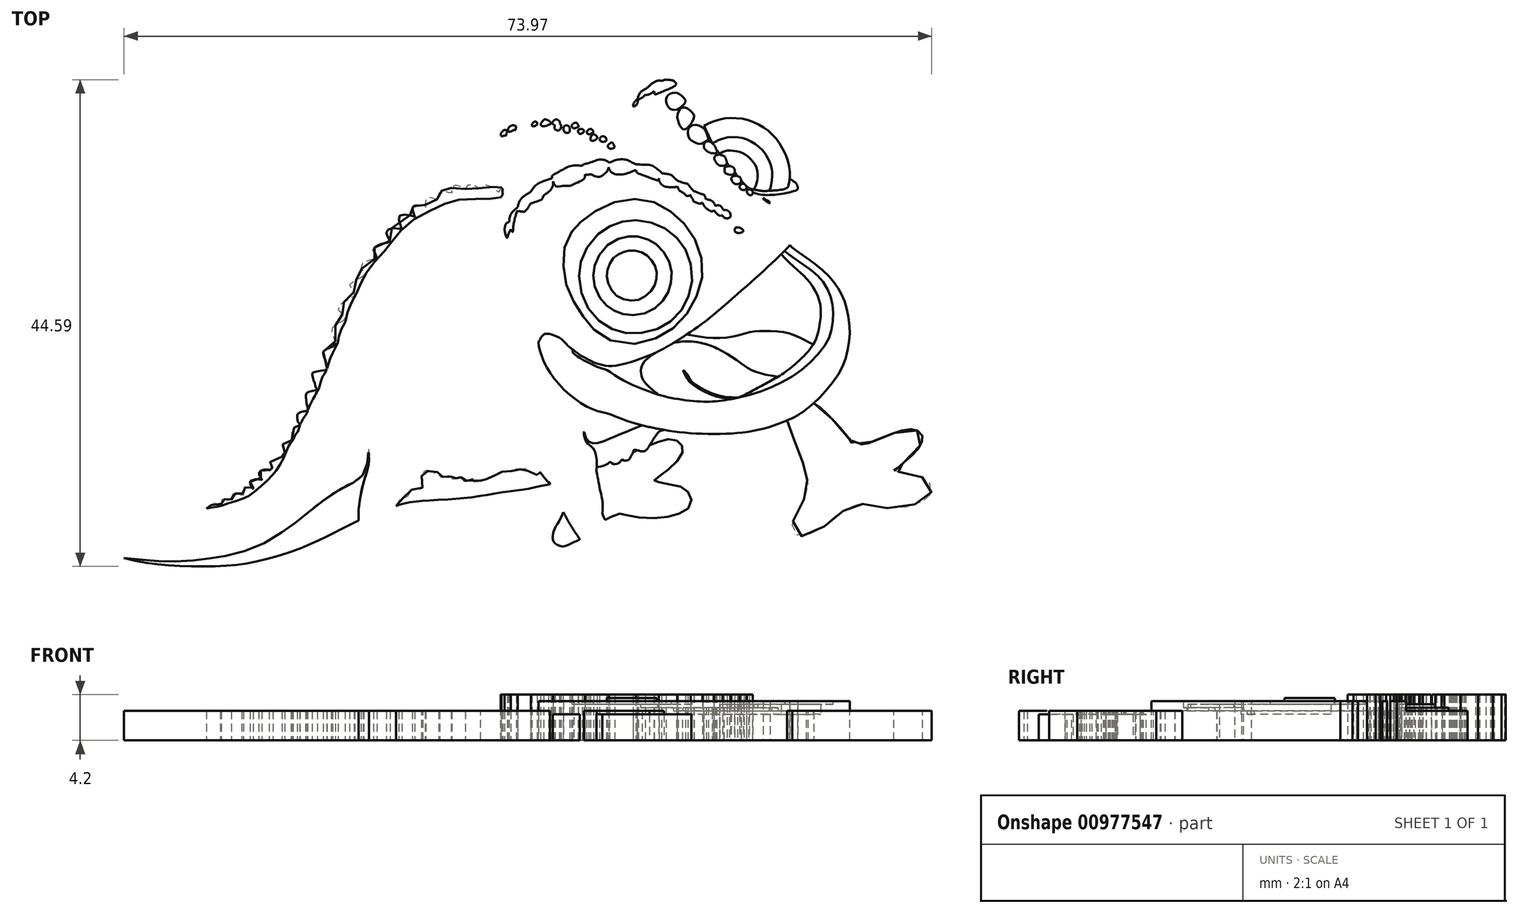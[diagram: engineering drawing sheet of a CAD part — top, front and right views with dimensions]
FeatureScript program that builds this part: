
annotation { "Feature Type Name" : "Feature", "Feature Type Description" : "" }
export const myFeature = defineFeature(function(context is Context, id is Id, definition is map)
    precondition{}
    {
        {
            var Q0;
            Q0=qCreatedBy(makeId("Top.planeOp"),FACE);
            var sketch = newSketch(context, id + "F0", { "sketchPlane" : qUnion([Q0])});
            skFitSpline(sketch, "E0", {"points": [v(3.36, 19.21) * mm, v(3.3, 19.55) * mm, v(3.25, 19.7) * mm, v(3.15, 20.16) * mm, v(3.22, 20.33) * mm, v(3.12, 20.54) * mm, v(3.1, 20.77) * mm, v(3.07, 20.9) * mm, v(3.13, 21.62) * mm, v(3.42, 22.28) * mm, v(3.48, 22.32) * mm, v(3.54, 22.32) * mm, v(3.5, 22.43) * mm, v(3.6, 22.71) * mm, v(3.91, 22.9) * mm, v(4.1, 22.82) * mm, v(4.13, 22.83) * mm, v(4.18, 23.04) * mm, v(4.6, 23.32) * mm, v(4.9, 23.23) * mm, v(4.98, 23.25) * mm, v(5.37, 23.44) * mm, v(5.56, 23.41) * mm, v(5.6, 23.45) * mm, v(5.75, 23.58) * mm, v(5.97, 23.6) * mm, v(6.16, 23.72) * mm, v(6.36, 23.71) * mm, v(6.58, 23.78) * mm, v(6.73, 23.79) * mm, v(6.85, 23.86) * mm, v(6.99, 23.79) * mm, v(7.13, 23.85) * mm, v(7.4, 23.84) * mm, v(7.43, 23.81) * mm, v(7.5, 23.85) * mm, v(7.77, 23.8) * mm, v(7.85, 23.77) * mm, v(7.97, 23.83) * mm, v(8.11, 23.77) * mm, v(8.21, 23.81) * mm, v(8.37, 23.77) * mm, v(8.6, 23.86) * mm, v(8.86, 23.7) * mm, v(8.96, 23.72) * mm, v(9.02, 23.7) * mm, v(9.66, 23.52) * mm, v(9.7, 23.5) * mm, v(9.8, 23.56) * mm, v(9.94, 23.45) * mm, v(10.06, 23.43) * mm, v(10.29, 23.54) * mm, v(10.47, 23.5) * mm, v(10.61, 23.3) * mm, v(10.72, 23.27) * mm, v(11.48, 22.95) * mm, v(11.55, 22.93) * mm, v(11.75, 22.98) * mm, v(11.93, 22.84) * mm, v(11.98, 22.73) * mm, v(12.04, 22.73) * mm, v(12.52, 22.87) * mm, v(14.39, 23.93) * mm, v(15.12, 24.58) * mm, v(15.61, 25.1) * mm, v(15.65, 25.3) * mm, v(16, 25.73) * mm, v(16.03, 25.76) * mm, v(16.1, 26.02) * mm, v(16.36, 26.4) * mm, v(16.61, 26.56) * mm, v(16.98, 26.8) * mm, v(17.36, 27.16) * mm, v(17.8, 27.38) * mm, v(18.13, 27.42) * mm, v(18.21, 27.39) * mm, v(18.5, 27.48) * mm, v(19.05, 27.46) * mm, v(19.4, 27.33) * mm, v(19.8, 26.81) * mm, v(19.97, 26.7) * mm, v(20.08, 26.52) * mm, v(20.3, 26.37) * mm, v(20.47, 26.08) * mm, v(20.68, 25.88) * mm, v(20.84, 25.53) * mm, v(20.98, 25.43) * mm, v(21.36, 24.69) * mm, v(21.85, 23.7) * mm, v(22.06, 23.33) * mm, v(22.1, 23.3) * mm, v(22.23, 23.34) * mm, v(22.63, 23.53) * mm, v(23.67, 23.88) * mm, v(24.92, 23.97) * mm, v(26.07, 23.82) * mm, v(27.24, 23.3) * mm, v(28.18, 22.64) * mm, v(28.92, 21.8) * mm, v(29.64, 20.47) * mm, v(29.96, 19.2) * mm, v(29.94, 18.42) * mm, v(29.95, 18.36) * mm, v(30.04, 18.34) * mm, v(30.26, 18.21) * mm, v(30.5, 18.03) * mm, v(30.66, 17.76) * mm, v(30.7, 17.54) * mm, v(30.7, 17.5) * mm, v(30.85, 17.46) * mm, v(31.15, 17.32) * mm, v(31.5, 16.97) * mm, v(31.79, 16.44) * mm, v(31.9, 15.87) * mm, v(31.7, 14.93) * mm, v(31.15, 13.83) * mm, v(30.33, 12.75) * mm, v(30, 12.37) * mm, v(29.98, 12.33) * mm, v(30.07, 12.21) * mm, v(31.05, 11.47) * mm, v(32.59, 10.36) * mm, v(33.74, 9.25) * mm, v(34.4, 8.36) * mm, v(34.9, 7.38) * mm, v(35.26, 6.15) * mm, v(35.44, 4.64) * mm, v(35.41, 3.6) * mm, v(35.09, 1.98) * mm, v(34.46, 0.58) * mm, v(33.14, -1.16) * mm, v(32.17, -2.13) * mm, v(31, -3.05) * mm, v(29.29, -3.9) * mm, v(26.88, -4.63) * mm, v(24.12, -4.95) * mm, v(20.81, -4.89) * mm, v(18.07, -4.53) * mm, v(14.95, -3.75) * mm, v(13.35, -3.12) * mm, v(12.18, -2.8) * mm, v(10.2, -1.7) * mm, v(8.22, 0.33) * mm, v(7.24, 2.16) * mm, v(6.96, 3.44) * mm, v(7.04, 4.02) * mm, v(6.96, 4.42) * mm, v(6.87, 4.52) * mm, v(6.86, 4.68) * mm, v(6.77, 4.8) * mm, v(6.81, 4.93) * mm, v(6.68, 5.06) * mm, v(6.64, 5.16) * mm, v(6.54, 5.27) * mm, v(6.53, 5.4) * mm, v(6.4, 5.52) * mm, v(6.4, 5.65) * mm, v(6.3, 5.75) * mm, v(6.28, 5.9) * mm, v(6.16, 5.97) * mm, v(6.05, 6.23) * mm, v(5.88, 6.37) * mm, v(5.87, 6.56) * mm, v(5.73, 6.72) * mm, v(5.53, 7.05) * mm, v(5.42, 7.08) * mm, v(5.38, 7.26) * mm, v(5.23, 7.33) * mm, v(5.18, 7.57) * mm, v(4.95, 7.62) * mm, v(4.85, 7.92) * mm, v(4.73, 8.04) * mm, v(4.57, 8.31) * mm, v(4.44, 8.38) * mm, v(4.25, 8.76) * mm, v(3.99, 9.34) * mm, v(3.65, 10.21) * mm, v(3.46, 10.94) * mm, v(3.4, 11.48) * mm, v(3.45, 12.23) * mm, v(3.5, 12.35) * mm, v(3.47, 12.52) * mm, v(3.5, 12.85) * mm, v(3.57, 12.92) * mm, v(3.52, 13.13) * mm, v(3.58, 13.32) * mm, v(3.55, 13.42) * mm, v(3.7, 13.73) * mm, v(3.62, 13.9) * mm, v(3.61, 14.08) * mm, v(3.74, 14.25) * mm, v(3.67, 14.43) * mm, v(3.67, 14.55) * mm, v(3.77, 14.7) * mm, v(3.7, 14.84) * mm, v(3.67, 15.05) * mm, v(3.72, 15.17) * mm, v(3.62, 15.47) * mm, v(3.58, 15.63) * mm, v(3.64, 15.75) * mm, v(3.56, 15.93) * mm, v(3.58, 16.1) * mm, v(3.67, 16.27) * mm, v(3.6, 16.48) * mm, v(3.51, 16.7) * mm, v(3.63, 16.91) * mm, v(3.66, 17.05) * mm, v(3.64, 17.33) * mm, v(3.68, 17.4) * mm, v(3.57, 17.6) * mm, v(3.5, 17.83) * mm, v(3.5, 18.02) * mm, v(3.44, 18.17) * mm, v(3.46, 18.36) * mm, v(3.4, 18.52) * mm, v(3.38, 18.72) * mm, v(3.43, 19) * mm, v(3.38, 19.14) * mm, v(3.36, 19.21) * mm]});
            skFitSpline(sketch, "E1", {"points": [v(22.1, 23.3) * mm, v(22.63, 22.16) * mm, v(22.8, 21.8) * mm, v(22.92, 21.6) * mm, v(23.04, 21.5) * mm, v(23.27, 21.02) * mm, v(23.33, 20.97) * mm, v(23.42, 20.86) * mm, v(23.43, 20.81) * mm, v(23.52, 20.76) * mm, v(23.54, 20.64) * mm, v(23.9, 20.52) * mm, v(24.12, 20.21) * mm, v(24.21, 19.89) * mm, v(24.3, 19.72) * mm, v(24.44, 19.57) * mm, v(24.55, 19.57) * mm, v(24.68, 19.51) * mm, v(24.82, 19.43) * mm, v(24.91, 19.22) * mm, v(24.93, 19.06) * mm, v(25.03, 18.86) * mm, v(25.16, 18.66) * mm, v(25.31, 18.62) * mm, v(25.42, 18.52) * mm, v(25.59, 18.16) * mm, v(25.84, 17.89) * mm, v(26.2, 17.57) * mm, v(26.8, 17.4) * mm, v(27.44, 17.3) * mm, v(28.2, 17.32) * mm, v(29.05, 17.4) * mm, v(29.64, 17.54) * mm, v(29.8, 17.65) * mm, v(29.84, 17.82) * mm, v(29.92, 18.2) * mm, v(29.95, 18.36) * mm], "startDerivative": vector(10.3, -22.36) * mm, "endDerivative": vector(1.64, 8.1) * mm});
            skFitSpline(sketch, "E2", {"points": [v(29.98, 12.33) * mm, v(29.51, 11.83) * mm, v(28.13, 10.5) * mm, v(25.13, 7.82) * mm, v(22.15, 5.3) * mm, v(20.12, 3.88) * mm, v(17.84, 2.57) * mm, v(15.15, 1.55) * mm, v(13.48, 1.25) * mm, v(12.74, 1.37) * mm, v(12, 1.6) * mm, v(10.98, 2.12) * mm, v(10.54, 2.43) * mm, v(10.18, 2.66) * mm, v(10.13, 2.66) * mm, v(10.04, 2.6) * mm, v(10.2, 2.38) * mm, v(10.67, 2.03) * mm, v(11.44, 1.6) * mm, v(12.67, 1.05) * mm, v(13.23, 0.87) * mm, v(14.13, 0.29) * mm, v(15.42, -0.41) * mm, v(16.91, -1.02) * mm, v(18.6, -1.56) * mm, v(21.65, -2) * mm, v(23.71, -1.92) * mm, v(26.07, -1.44) * mm, v(28.23, -0.7) * mm, v(30.3, 0.4) * mm, v(32.04, 1.78) * mm, v(33.3, 3.33) * mm, v(33.76, 4.53) * mm, v(33.95, 5.87) * mm, v(33.86, 6.97) * mm, v(33.54, 8.03) * mm, v(32.86, 9.18) * mm, v(31.95, 10) * mm, v(30.53, 11) * mm, v(29.72, 11.6) * mm, v(29.52, 11.77) * mm], "startDerivative": vector(-23.28, -25.11) * mm, "endDerivative": vector(-11.86, 14.14) * mm});
            skLineSegment(sketch, "E3", {"start": v(29.52, 11.77) * mm, "end": v(29.49, 11.8) * mm});
            skFitSpline(sketch, "E4", {"points": [v(14.66, 14.5) * mm, v(15.84, 14.61) * mm, v(17.45, 14.33) * mm, v(18.8, 13.67) * mm, v(19.97, 12.58) * mm, v(20.68, 11.35) * mm, v(21.02, 9.5) * mm, v(20.74, 7.86) * mm, v(20, 6.32) * mm, v(18.77, 5.13) * mm, v(17.34, 4.47) * mm, v(15.5, 4.25) * mm, v(14.1, 4.48) * mm, v(12.62, 5.29) * mm, v(11.45, 6.62) * mm, v(10.75, 8.45) * mm, v(10.7, 10.2) * mm, v(11.12, 11.62) * mm, v(12.32, 13.24) * mm, v(13.54, 14.1) * mm, v(14.66, 14.5) * mm]});
            skFitSpline(sketch, "E5", {"points": [v(32.17, -2.13) * mm, v(32.66, -2.47) * mm, v(33.56, -3.33) * mm, v(34.46, -4.25) * mm, v(35.37, -5.35) * mm, v(35.6, -5.72) * mm, v(35.62, -5.76) * mm, v(35.7, -5.73) * mm, v(35.9, -5.68) * mm, v(36.13, -5.73) * mm, v(36.33, -5.84) * mm, v(36.4, -5.98) * mm, v(36.46, -5.93) * mm, v(36.76, -5.9) * mm, v(37.41, -5.73) * mm, v(38.35, -5.32) * mm, v(39.02, -5.08) * mm, v(40.07, -4.7) * mm, v(41.05, -4.51) * mm, v(41.64, -4.66) * mm, v(42.03, -5.01) * mm, v(42.12, -5.37) * mm, v(41.98, -5.9) * mm, v(41.47, -6.63) * mm, v(40.62, -7.4) * mm, v(39.86, -8.06) * mm, v(39.55, -8.27) * mm, v(39.5, -8.3) * mm, v(39.65, -8.33) * mm, v(40.23, -8.53) * mm, v(41.69, -8.82) * mm, v(42.1, -8.96) * mm, v(42.58, -9.3) * mm, v(42.9, -9.78) * mm, v(42.93, -10.3) * mm, v(42.71, -10.8) * mm, v(42.22, -11.1) * mm, v(40.92, -11.59) * mm, v(39.88, -11.76) * mm, v(38.26, -11.7) * mm, v(37.2, -11.47) * mm, v(36.6, -11.38) * mm, v(36.05, -11.41) * mm, v(35.23, -11.8) * mm, v(34.58, -12.19) * mm, v(33.75, -12.9) * mm, v(32.97, -13.54) * mm, v(31.99, -14.05) * mm, v(31.12, -14.34) * mm, v(30.45, -14.13) * mm, v(30.21, -13.6) * mm, v(30.29, -12.83) * mm, v(30.8, -11.93) * mm, v(31.26, -10.99) * mm, v(31.59, -9.9) * mm, v(31.66, -9.54) * mm, v(31.57, -9.26) * mm, v(31.48, -8.78) * mm, v(31.46, -8.26) * mm, v(31.25, -7.84) * mm, v(30.85, -6.89) * mm, v(30.46, -5.85) * mm, v(30.21, -5.05) * mm, v(29.84, -4.02) * mm, v(29.72, -3.77) * mm, v(29.7, -3.74) * mm], "startDerivative": vector(30.93, -18.84) * mm, "endDerivative": vector(-5.35, 12.51) * mm});
            skFitSpline(sketch, "E6", {"points": [v(17.12, -6.01) * mm, v(17.73, -5.76) * mm, v(18.57, -5.48) * mm, v(19.33, -5.47) * mm, v(19.77, -5.69) * mm, v(20.08, -6.02) * mm, v(20.15, -6.39) * mm, v(20.1, -6.84) * mm, v(19.51, -7.6) * mm, v(18.62, -8.4) * mm, v(18.03, -8.84) * mm, v(17.63, -9.17) * mm, v(17.54, -9.24) * mm, v(17.63, -9.27) * mm, v(18.1, -9.43) * mm, v(19.26, -9.64) * mm, v(20.04, -9.84) * mm, v(20.55, -10.2) * mm, v(20.91, -10.73) * mm, v(20.87, -11.47) * mm, v(20.4, -12.02) * mm, v(19.4, -12.4) * mm, v(18.3, -12.63) * mm, v(16.43, -12.66) * mm, v(15.3, -12.46) * mm, v(14.56, -12.28) * mm, v(14.24, -12.3) * mm, v(13.48, -12.61) * mm, v(13.09, -12.83) * mm, v(13.05, -12.85) * mm, v(13, -12.75) * mm, v(12.81, -12.3) * mm, v(12.84, -11.66) * mm, v(12.68, -10.48) * mm, v(12.51, -9.74) * mm, v(12.3, -8.63) * mm, v(12.27, -8.08) * mm, v(12.62, -7.95) * mm, v(13.14, -7.8) * mm, v(13.44, -7.59) * mm, v(13.56, -7.54) * mm, v(13.75, -7.71) * mm, v(14.05, -7.72) * mm, v(14.36, -7.6) * mm, v(14.49, -7.41) * mm, v(14.6, -7.33) * mm, v(14.86, -7.43) * mm, v(15.06, -7.39) * mm, v(15.28, -7.28) * mm, v(15.4, -7.05) * mm, v(15.6, -6.64) * mm, v(15.67, -6.45) * mm, v(15.96, -6.45) * mm, v(16.43, -6.57) * mm, v(16.74, -6.49) * mm, v(17.02, -6.17) * mm, v(17.12, -6.01) * mm]});
            skFitSpline(sketch, "E7", {"points": [v(9.21, -12.15) * mm, v(9.2, -12.22) * mm, v(9.07, -12.5) * mm, v(8.76, -13.09) * mm, v(8.46, -13.57) * mm, v(8.31, -13.98) * mm, v(8.24, -14.5) * mm, v(8.37, -14.88) * mm, v(8.7, -15.16) * mm, v(9.26, -15.28) * mm, v(9.8, -15.08) * mm, v(10.35, -14.81) * mm, v(10.7, -14.65) * mm, v(10.74, -14.63) * mm, v(10.7, -14.57) * mm, v(10.4, -14.15) * mm, v(10.02, -13.55) * mm, v(9.7, -13.03) * mm, v(9.44, -12.53) * mm, v(9.26, -12.19) * mm, v(9.21, -12.15) * mm]});
            skFitSpline(sketch, "E8", {"points": [v(15.6, -6.64) * mm, v(15.8, -6.57) * mm, v(16.01, -6.47) * mm], "startDerivative": vector(0.38, 0.15) * mm, "endDerivative": vector(0.42, 0.2) * mm});
            skFitSpline(sketch, "E9", {"points": [v(17.12, -6.01) * mm, v(17.35, -5.63) * mm, v(17.7, -5.12) * mm, v(17.96, -4.79) * mm, v(18.2, -4.65) * mm, v(18.43, -4.6) * mm], "startDerivative": vector(0.97, 1.7) * mm, "endDerivative": vector(1.43, 0.4) * mm});
            skFitSpline(sketch, "E10", {"points": [v(13.05, -12.85) * mm, v(13.4, -13.6) * mm, v(13.92, -14.65) * mm, v(14.3, -15.25) * mm, v(14.83, -15.89) * mm, v(15.55, -16.82) * mm, v(16.03, -17.45) * mm, v(16.54, -17.98) * mm, v(16.8, -18.2) * mm, v(17.09, -18.54) * mm, v(17.3, -18.9) * mm, v(17.49, -19.25) * mm, v(17.59, -19.46) * mm, v(17.62, -19.5) * mm, v(17.72, -19.53) * mm, v(18, -19.74) * mm, v(18.29, -19.92) * mm, v(18.67, -20.05) * mm, v(19.2, -20.03) * mm, v(19.94, -19.97) * mm, v(20.93, -19.76) * mm, v(21.74, -19.57) * mm, v(22.27, -19.59) * mm, v(22.65, -19.68) * mm, v(22.95, -19.84) * mm, v(23.17, -20.07) * mm, v(23.28, -20.35) * mm, v(23.28, -20.67) * mm, v(23.22, -20.88) * mm, v(23.06, -21.2) * mm, v(22.46, -21.93) * mm, v(21.92, -22.64) * mm, v(21.26, -23.31) * mm, v(20.64, -23.75) * mm, v(20.04, -24.22) * mm, v(19.43, -24.8) * mm, v(18.99, -25.18) * mm, v(18.86, -25.3) * mm, v(18.75, -25.6) * mm, v(18.7, -25.98) * mm, v(18.6, -26.82) * mm, v(18.33, -27.68) * mm, v(17.88, -28.37) * mm, v(17.35, -28.83) * mm, v(16.71, -29.2) * mm, v(15.83, -29.46) * mm, v(14.95, -29.4) * mm, v(14.37, -29.2) * mm, v(14.03, -28.71) * mm, v(13.97, -28.15) * mm, v(14.14, -27.4) * mm, v(14.28, -26.68) * mm, v(14.27, -26.65) * mm, v(14.1, -26.73) * mm, v(13.35, -26.98) * mm, v(12.23, -27.26) * mm, v(11, -27.52) * mm, v(9.8, -27.57) * mm, v(9.23, -27.47) * mm, v(8.95, -27.22) * mm, v(8.84, -26.8) * mm, v(8.94, -26.3) * mm, v(9.22, -25.87) * mm, v(9.74, -25.46) * mm, v(10.36, -25.07) * mm, v(10.86, -24.7) * mm, v(11.47, -24.33) * mm, v(12.13, -23.97) * mm, v(12.7, -23.65) * mm, v(13.1, -23.33) * mm, v(13.25, -23.2) * mm, v(13.23, -23.14) * mm, v(13.22, -22.92) * mm, v(13.28, -22.58) * mm, v(13.35, -22.43) * mm, v(13.33, -22.39) * mm, v(13.11, -22) * mm, v(12.81, -21.3) * mm, v(12.64, -20.71) * mm, v(12.4, -20.15) * mm, v(12, -19.22) * mm, v(11.67, -18.32) * mm, v(11.44, -17.49) * mm, v(11.32, -16.6) * mm, v(11.27, -16.02) * mm, v(11.3, -15.63) * mm, v(11.27, -15.57) * mm, v(11.04, -15.1) * mm, v(10.85, -14.79) * mm, v(10.74, -14.63) * mm], "startDerivative": vector(22.88, -50.93) * mm, "endDerivative": vector(-15.94, 22.2) * mm});
            skFitSpline(sketch, "E11", {"points": [v(3.57, 17.6) * mm, v(3.52, 17.54) * mm, v(3.53, 17.45) * mm, v(3.49, 17.4) * mm, v(3.38, 17.33) * mm, v(3.32, 17.22) * mm, v(3.31, 17.15) * mm, v(3.29, 17.18) * mm, v(3.06, 17.4) * mm, v(2.58, 17.76) * mm, v(2.2, 17.83) * mm, v(1.9, 17.75) * mm, v(1.73, 17.55) * mm, v(1.69, 17.46) * mm, v(1.67, 17.4) * mm, v(1.6, 17.47) * mm, v(1.42, 17.58) * mm, v(1.06, 17.8) * mm, v(0.78, 17.87) * mm, v(0.5, 17.83) * mm, v(0.33, 17.74) * mm, v(0.26, 17.58) * mm, v(0.26, 17.47) * mm, v(0.24, 17.46) * mm, v(0.13, 17.52) * mm, v(-0.08, 17.67) * mm, v(-0.42, 17.8) * mm, v(-0.75, 17.81) * mm, v(-0.93, 17.72) * mm, v(-1.04, 17.6) * mm, v(-1.06, 17.37) * mm, v(-1, 17.1) * mm, v(-1, 16.96) * mm, v(-1.02, 16.98) * mm, v(-1.44, 17.24) * mm, v(-1.76, 17.34) * mm, v(-2, 17.3) * mm, v(-2.15, 17.16) * mm, v(-2.2, 16.9) * mm, v(-2.16, 16.58) * mm, v(-2.13, 16.41) * mm, v(-2.12, 16.37) * mm, v(-2.17, 16.41) * mm, v(-2.28, 16.49) * mm, v(-2.72, 16.66) * mm, v(-3.11, 16.66) * mm, v(-3.29, 16.6) * mm, v(-3.4, 16.49) * mm, v(-3.43, 16.38) * mm, v(-3.45, 16.17) * mm, v(-3.4, 15.92) * mm, v(-3.37, 15.82) * mm, v(-3.37, 15.79) * mm, v(-3.45, 15.83) * mm, v(-3.67, 15.9) * mm, v(-4, 16) * mm, v(-4.33, 15.97) * mm, v(-4.54, 15.86) * mm, v(-4.6, 15.72) * mm, v(-4.61, 15.55) * mm, v(-4.52, 15.3) * mm, v(-4.43, 15.09) * mm, v(-4.38, 14.95) * mm, v(-4.4, 14.96) * mm, v(-4.75, 15.04) * mm, v(-5.13, 15.11) * mm, v(-5.5, 15.11) * mm, v(-5.72, 15.04) * mm, v(-5.8, 14.93) * mm, v(-5.85, 14.76) * mm, v(-5.8, 14.5) * mm, v(-5.71, 14.22) * mm, v(-5.6, 13.94) * mm, v(-5.58, 13.84) * mm, v(-5.57, 13.8) * mm, v(-5.61, 13.79) * mm, v(-5.8, 13.82) * mm, v(-6.24, 13.9) * mm, v(-6.6, 13.85) * mm, v(-6.86, 13.73) * mm, v(-6.97, 13.6) * mm, v(-7, 13.45) * mm, v(-6.91, 13.2) * mm, v(-6.76, 12.92) * mm, v(-6.67, 12.7) * mm, v(-6.65, 12.64) * mm, v(-6.7, 12.62) * mm, v(-6.93, 12.54) * mm, v(-7.38, 12.45) * mm, v(-7.7, 12.33) * mm, v(-8.01, 12.18) * mm, v(-8.12, 12.07) * mm, v(-8.15, 11.9) * mm, v(-8.1, 11.77) * mm, v(-7.97, 11.44) * mm, v(-7.85, 11.2) * mm, v(-7.87, 11.18) * mm, v(-7.97, 11.13) * mm, v(-8, 11.09) * mm, v(-8.06, 11.05) * mm, v(-8.25, 11.01) * mm, v(-8.64, 10.93) * mm, v(-9.11, 10.7) * mm, v(-9.24, 10.56) * mm, v(-9.3, 10.36) * mm, v(-9.25, 10.14) * mm, v(-9.09, 9.82) * mm, v(-9.05, 9.68) * mm, v(-9.09, 9.58) * mm, v(-9.13, 9.46) * mm, v(-9.14, 9.4) * mm, v(-9.23, 9.36) * mm, v(-9.67, 9.17) * mm, v(-10.06, 8.98) * mm, v(-10.26, 8.85) * mm, v(-10.35, 8.69) * mm, v(-10.34, 8.47) * mm, v(-10.16, 8.26) * mm, v(-10.06, 8.13) * mm, v(-9.9, 7.89) * mm, v(-9.91, 7.83) * mm, v(-9.95, 7.76) * mm, v(-9.95, 7.64) * mm, v(-10, 7.6) * mm, v(-10.1, 7.54) * mm, v(-10.54, 7.34) * mm, v(-10.87, 7.12) * mm, v(-11.1, 6.94) * mm, v(-11.3, 6.77) * mm, v(-11.4, 6.62) * mm, v(-11.41, 6.48) * mm, v(-11.3, 6.27) * mm, v(-11.11, 6.07) * mm, v(-10.9, 5.82) * mm, v(-10.77, 5.66) * mm, v(-10.76, 5.63) * mm, v(-10.78, 5.6) * mm, v(-10.87, 5.47) * mm, v(-11, 5.36) * mm, v(-11.44, 5.14) * mm, v(-11.77, 4.87) * mm, v(-11.99, 4.68) * mm, v(-12.05, 4.47) * mm, v(-11.96, 4.23) * mm, v(-11.8, 3.9) * mm, v(-11.7, 3.58) * mm, v(-11.66, 3.5) * mm, v(-11.76, 3.22) * mm, v(-11.82, 3.07) * mm, v(-11.95, 3.02) * mm, v(-12.23, 2.9) * mm, v(-12.58, 2.72) * mm, v(-12.77, 2.53) * mm, v(-12.73, 2.24) * mm, v(-12.6, 1.86) * mm, v(-12.5, 1.6) * mm, v(-12.47, 1.37) * mm, v(-12.45, 1.2) * mm, v(-12.43, 1.03) * mm, v(-12.52, 0.92) * mm, v(-12.78, 0.84) * mm, v(-13.28, 0.78) * mm, v(-13.61, 0.68) * mm, v(-13.73, 0.64) * mm, v(-13.77, 0.52) * mm, v(-13.72, 0.24) * mm, v(-13.63, -0.09) * mm, v(-13.52, -0.41) * mm, v(-13.47, -0.7) * mm, v(-13.36, -0.8) * mm, v(-13.3, -0.92) * mm, v(-13.46, -0.98) * mm, v(-13.8, -1.03) * mm, v(-14.15, -1.14) * mm, v(-14.31, -1.26) * mm, v(-14.37, -1.43) * mm, v(-14.37, -1.6) * mm, v(-14.3, -1.98) * mm, v(-14.28, -2.27) * mm, v(-14.19, -2.5) * mm, v(-14.21, -2.7) * mm, v(-14.2, -2.83) * mm, v(-14.34, -2.87) * mm, v(-14.68, -2.93) * mm, v(-14.97, -3.04) * mm, v(-15.13, -3.2) * mm, v(-15.15, -3.5) * mm, v(-15.09, -3.83) * mm, v(-14.98, -4) * mm, v(-14.9, -4.08) * mm, v(-14.89, -4.13) * mm, v(-14.94, -4.16) * mm, v(-14.93, -4.22) * mm, v(-15, -4.24) * mm, v(-15.33, -4.36) * mm, v(-15.62, -4.54) * mm, v(-15.7, -4.72) * mm, v(-15.64, -5.05) * mm, v(-15.54, -5.33) * mm, v(-15.6, -5.35) * mm, v(-15.64, -5.4) * mm, v(-15.68, -5.48) * mm, v(-15.66, -5.55) * mm, v(-15.7, -5.55) * mm, v(-16.1, -5.72) * mm, v(-16.42, -5.89) * mm, v(-16.54, -6.03) * mm, v(-16.48, -6.27) * mm, v(-16.34, -6.6) * mm, v(-16.3, -6.74) * mm, v(-16.42, -6.83) * mm, v(-16.46, -6.92) * mm, v(-16.48, -7.02) * mm, v(-16.72, -7.12) * mm, v(-17.43, -7.4) * mm, v(-17.66, -7.58) * mm, v(-17.74, -7.71) * mm, v(-17.67, -7.9) * mm, v(-17.5, -8) * mm, v(-17.4, -8.15) * mm, v(-17.4, -8.24) * mm, v(-17.47, -8.22) * mm, v(-17.5, -8.26) * mm, v(-17.55, -8.3) * mm, v(-17.77, -8.25) * mm, v(-18.1, -8.22) * mm, v(-18.39, -8.3) * mm, v(-18.6, -8.43) * mm, v(-18.66, -8.62) * mm, v(-18.56, -8.86) * mm, v(-18.41, -9.08) * mm, v(-18.39, -9.17) * mm, v(-18.45, -9.17) * mm, v(-18.73, -9.13) * mm, v(-18.96, -9.13) * mm, v(-19.19, -9.18) * mm, v(-19.42, -9.27) * mm, v(-19.48, -9.4) * mm, v(-19.4, -9.63) * mm, v(-19.26, -9.82) * mm, v(-19.2, -9.85) * mm, v(-19.18, -9.92) * mm, v(-19.21, -10) * mm, v(-19.34, -9.95) * mm, v(-19.8, -9.87) * mm, v(-20.1, -9.9) * mm, v(-20.21, -10.03) * mm, v(-20.19, -10.3) * mm, v(-20.06, -10.57) * mm, v(-20.14, -10.62) * mm, v(-20.82, -10.45) * mm, v(-20.95, -10.45) * mm, v(-21.13, -10.56) * mm, v(-21.19, -10.82) * mm, v(-21.21, -11.06) * mm, v(-21.33, -11.14) * mm, v(-21.53, -11.05) * mm, v(-21.86, -10.95) * mm, v(-22, -10.97) * mm, v(-22.09, -11.05) * mm, v(-22.12, -11.26) * mm, v(-22.11, -11.4) * mm, v(-22.16, -11.4) * mm, v(-22.21, -11.44) * mm, v(-22.2, -11.5) * mm, v(-22.25, -11.52) * mm, v(-22.32, -11.45) * mm, v(-22.62, -11.35) * mm, v(-22.76, -11.33) * mm, v(-22.95, -11.43) * mm, v(-23.08, -11.52) * mm, v(-23.32, -11.68) * mm, v(-23.43, -11.7) * mm, v(-23.49, -11.75) * mm, v(-23.47, -11.81) * mm, v(-23.53, -11.8) * mm, v(-23.64, -11.82) * mm, v(-23.78, -11.89) * mm, v(-24.05, -11.84) * mm, v(-24.3, -11.92) * mm, v(-24.4, -11.88) * mm, v(-24.63, -11.98) * mm, v(-24.71, -11.9) * mm, v(-24.86, -11.91) * mm, v(-24.9, -12.01) * mm, v(-25.01, -12.03) * mm, v(-25.1, -11.94) * mm, v(-25.26, -12.04) * mm, v(-25.39, -11.98) * mm, v(-25.62, -12.1) * mm, v(-25.75, -12.04) * mm, v(-25.92, -12.12) * mm, v(-26.11, -12.09) * mm, v(-26.25, -12.18) * mm, v(-26.37, -12.09) * mm, v(-26.52, -12.2) * mm, v(-26.67, -12.13) * mm, v(-26.78, -12.21) * mm, v(-26.95, -12.13) * mm, v(-27.1, -12.22) * mm, v(-27.38, -12.16) * mm, v(-27.88, -12.17) * mm, v(-28.73, -12.12) * mm, v(-30.06, -11.96) * mm, v(-31.97, -11.46) * mm, v(-34.52, -10.39) * mm, v(-36.83, -8.78) * mm, v(-38.21, -7.47) * mm, v(-39.16, -6.46) * mm, v(-40.37, -5.2) * mm, v(-41.08, -4.16) * mm, v(-41.6, -2.48) * mm, v(-41.47, -0.75) * mm, v(-41.01, 0.46) * mm, v(-40.08, 1.58) * mm, v(-39, 2.24) * mm, v(-38.02, 2.54) * mm, v(-36.34, 2.46) * mm, v(-35.03, 1.53) * mm, v(-34.26, 0.26) * mm, v(-34.01, -1.1) * mm, v(-34.2, -2.59) * mm, v(-35.31, -4.2) * mm, v(-36.95, -4.68) * mm, v(-38.44, -4.23) * mm, v(-39.01, -3.73) * mm, v(-39.59, -2.54) * mm, v(-39.53, -1) * mm, v(-38.9, 0.08) * mm, v(-37.9, 0.66) * mm, v(-36.77, 0.77) * mm, v(-35.91, 0.43) * mm, v(-35.48, -0.31) * mm, v(-35.5, -1.66) * mm, v(-36.28, -2.73) * mm, v(-37.38, -2.75) * mm, v(-37.82, -2.26) * mm, v(-37.88, -1.6) * mm, v(-37.54, -1.27) * mm, v(-37.06, -1.1) * mm, v(-36.8, -1.2) * mm, v(-36.27, -1.66) * mm, v(-35.87, -1.68) * mm, v(-35.65, -1.43) * mm, v(-35.64, -0.76) * mm, v(-35.82, -0.04) * mm, v(-36.19, 0.36) * mm, v(-36.91, 0.57) * mm, v(-37.83, 0.44) * mm, v(-38.68, -0.03) * mm, v(-39.08, -0.53) * mm, v(-39.35, -1.16) * mm, v(-39.46, -1.88) * mm, v(-39.3, -2.84) * mm, v(-39.02, -3.42) * mm, v(-38.45, -4) * mm, v(-37.62, -4.36) * mm, v(-36.75, -4.5) * mm, v(-35.98, -4.33) * mm, v(-35.06, -3.67) * mm, v(-34.34, -2.36) * mm, v(-34.2, -1.2) * mm, v(-34.36, -0.07) * mm, v(-34.74, 0.75) * mm, v(-35.21, 1.38) * mm, v(-35.77, 1.89) * mm, v(-36.96, 2.38) * mm, v(-38.1, 2.3) * mm, v(-39.01, 1.98) * mm, v(-39.98, 1.36) * mm, v(-40.55, 0.77) * mm, v(-41.03, -0.14) * mm, v(-41.34, -1.37) * mm, v(-41.33, -2.6) * mm, v(-41.13, -3.45) * mm, v(-40.67, -4.43) * mm, v(-40.05, -5.14) * mm, v(-39.24, -5.7) * mm, v(-38.43, -6.32) * mm, v(-37.69, -6.53) * mm, v(-36.28, -6.5) * mm, v(-34.91, -5.99) * mm, v(-33.87, -5.2) * mm, v(-32.94, -4.12) * mm, v(-32.32, -2.9) * mm, v(-32, -1.55) * mm, v(-32.06, -0.3) * mm, v(-32.37, 0.73) * mm, v(-33.02, 1.96) * mm, v(-33.95, 3.1) * mm, v(-35.61, 4.17) * mm, v(-37.45, 4.65) * mm, v(-38.95, 4.53) * mm, v(-40.38, 3.92) * mm, v(-41.78, 2.85) * mm, v(-43, 1.36) * mm, v(-43.76, -0.34) * mm, v(-44.1, -1.99) * mm, v(-44.05, -3.78) * mm, v(-43.75, -5.15) * mm, v(-43.36, -6.12) * mm, v(-42.55, -7.73) * mm, v(-41.1, -9.75) * mm, v(-39.56, -11.44) * mm, v(-37.6, -13.16) * mm, v(-34.73, -14.91) * mm, v(-32, -16.05) * mm, v(-28.66, -16.83) * mm, v(-25.3, -17.08) * mm, v(-21.68, -17.05) * mm, v(-18.98, -16.68) * mm, v(-15.36, -15.63) * mm, v(-13.02, -14.64) * mm, v(-11.48, -13.9) * mm, v(-9.8, -13.03) * mm, v(-9.58, -13) * mm, v(-9.54, -13.12) * mm, v(-9.57, -13.36) * mm, v(-9.45, -13.7) * mm, v(-9.44, -14.1) * mm, v(-9.44, -14.66) * mm, v(-9.5, -15.94) * mm, v(-9.57, -16.93) * mm, v(-9.67, -17.76) * mm, v(-9.72, -18.37) * mm, v(-9.72, -18.6) * mm, v(-9.84, -19.17) * mm, v(-10.05, -19.68) * mm, v(-10.15, -20.02) * mm, v(-10.17, -20.46) * mm, v(-10.15, -20.68) * mm, v(-10.35, -20.93) * mm, v(-10.73, -21.2) * mm, v(-11.12, -21.54) * mm, v(-11.55, -21.92) * mm, v(-11.87, -22.23) * mm, v(-12.23, -22.49) * mm, v(-12.59, -22.7) * mm, v(-13.09, -23.2) * mm, v(-13.13, -23.25) * mm, v(-13.61, -23.63) * mm, v(-13.96, -24.1) * mm, v(-14.25, -24.64) * mm, v(-14.3, -25.04) * mm, v(-14.33, -25.5) * mm, v(-14.15, -25.93) * mm, v(-13.9, -26.12) * mm, v(-13.34, -26.23) * mm, v(-12.48, -26.03) * mm, v(-11.67, -25.73) * mm, v(-11, -25.49) * mm, v(-10.35, -25.24) * mm, v(-9.7, -25) * mm, v(-8.96, -24.7) * mm, v(-8.4, -24.41) * mm, v(-8.1, -24.27) * mm, v(-7.93, -24.3) * mm, v(-7.9, -24.34) * mm, v(-7.88, -24.48) * mm, v(-7.99, -25.01) * mm, v(-8.08, -25.67) * mm, v(-8.19, -26.35) * mm, v(-8.22, -26.93) * mm, v(-8.07, -27.42) * mm, v(-7.64, -27.87) * mm, v(-6.92, -28.02) * mm, v(-6.25, -27.96) * mm, v(-5.56, -27.72) * mm, v(-5.01, -27.3) * mm, v(-4.42, -26.6) * mm, v(-3.96, -25.86) * mm, v(-3.74, -25.18) * mm, v(-3.62, -24.24) * mm, v(-3.53, -23.6) * mm, v(-3.35, -23.26) * mm, v(-2.97, -22.97) * mm, v(-1.99, -22.32) * mm, v(-1.18, -21.71) * mm, v(-0.64, -21.25) * mm, v(-0.06, -20.64) * mm, v(0.27, -20.16) * mm, v(0.46, -19.77) * mm, v(0.52, -19.2) * mm, v(0.37, -18.78) * mm, v(0.17, -18.47) * mm, v(-0.05, -18.22) * mm, v(-0.51, -17.98) * mm, v(-1.38, -17.88) * mm, v(-2.1, -17.95) * mm, v(-2.76, -17.98) * mm, v(-3.05, -18) * mm, v(-3.36, -18.06) * mm, v(-3.57, -18.12) * mm, v(-3.67, -18.18) * mm, v(-3.71, -18.16) * mm, v(-3.84, -18.05) * mm, v(-4.06, -17.94) * mm, v(-4.29, -17.9) * mm, v(-4.4, -17.87) * mm, v(-4.42, -17.82) * mm, v(-4.73, -17.09) * mm, v(-5.12, -16.18) * mm, v(-5.54, -15.24) * mm, v(-5.73, -14.79) * mm, v(-5.91, -14.5) * mm, v(-6.3, -13.95) * mm, v(-6.47, -13.63) * mm, v(-6.44, -13.48) * mm, v(-6.3, -12.86) * mm, v(-6.27, -12.28) * mm, v(-6.2, -11.8) * mm, v(-6.1, -11.58) * mm, v(-6, -11.54) * mm, v(-5.66, -11.41) * mm, v(-4.86, -11.24) * mm, v(-4, -11.13) * mm, v(-2.95, -11.05) * mm, v(-1.08, -10.95) * mm, v(0.19, -10.84) * mm, v(1.65, -10.65) * mm, v(2.86, -10.45) * mm, v(4.39, -10.2) * mm, v(5.4, -10.08) * mm, v(5.46, -10.07) * mm, v(6.52, -9.89) * mm, v(7.13, -9.75) * mm, v(7.8, -9.61) * mm, v(8, -9.57) * mm, v(8.04, -9.58) * mm, v(8.06, -9.6) * mm, v(8.26, -10.05) * mm, v(8.6, -10.79) * mm, v(8.94, -11.59) * mm, v(9.18, -12.07) * mm, v(9.21, -12.15) * mm], "startDerivative": vector(-73.71, -74.35) * mm, "endDerivative": vector(29.07, -74.8) * mm});
            skFitSpline(sketch, "E12", {"points": [v(-6.1, -11.58) * mm, v(-5.91, -11.3) * mm, v(-5.68, -10.96) * mm, v(-4.96, -10.6) * mm, v(-4.69, -10.08) * mm, v(-4.2, -10.03) * mm, v(-3.7, -9.9) * mm, v(-3.66, -9.47) * mm, v(-3.76, -8.85) * mm, v(-3.6, -8.5) * mm, v(-3.28, -8.27) * mm, v(-2.97, -8.54) * mm, v(-2.5, -8.48) * mm, v(-2.3, -8.47) * mm, v(-2.1, -8.62) * mm, v(-2.02, -8.8) * mm, v(-1.77, -8.9) * mm, v(-1.37, -8.82) * mm, v(-1.22, -8.77) * mm, v(-1.07, -8.92) * mm, v(-1.03, -9.04) * mm, v(-0.8, -9.1) * mm, v(-0.62, -9.02) * mm, v(-0.53, -9) * mm, v(-0.4, -8.92) * mm, v(-0.25, -8.86) * mm, v(-0.16, -8.94) * mm, v(-0.1, -9.03) * mm, v(0.04, -9.13) * mm, v(0.16, -9.24) * mm, v(0.52, -9.23) * mm, v(0.76, -9.17) * mm, v(0.87, -9.12) * mm, v(0.98, -9.25) * mm, v(1.17, -9.32) * mm, v(1.41, -9.36) * mm, v(1.63, -9.24) * mm, v(1.65, -9.12) * mm, v(1.89, -9.13) * mm, v(2.03, -9.14) * mm, v(2.34, -9.1) * mm, v(2.64, -8.93) * mm, v(2.98, -8.75) * mm, v(3.27, -8.7) * mm, v(3.5, -8.47) * mm, v(3.8, -8.4) * mm, v(4.12, -8.35) * mm, v(4.57, -8.35) * mm, v(4.87, -8.16) * mm, v(5.19, -8.2) * mm, v(5.52, -8.15) * mm, v(5.73, -8.13) * mm, v(5.92, -8.3) * mm, v(6.18, -8.5) * mm, v(6.61, -8.7) * mm, v(6.94, -8.64) * mm, v(6.96, -8.41) * mm, v(7.07, -8.41) * mm, v(7.11, -8.49) * mm, v(7.2, -8.72) * mm, v(7.51, -8.98) * mm, v(7.6, -9.15) * mm, v(7.8, -9.34) * mm, v(7.95, -9.42) * mm, v(8, -9.57) * mm], "startDerivative": vector(12, 14.87) * mm, "endDerivative": vector(3.03, -14.27) * mm});
            skLineSegment(sketch, "E13", {"start": v(-9.8, -13.03) * mm, "end": v(-9.53, -12.91) * mm});
            skLineSegment(sketch, "E14", {"start": v(-9.53, -12.91) * mm, "end": v(-9.54, -13.12) * mm});
            skFitSpline(sketch, "E15", {"points": [v(22.87, 21.66) * mm, v(23.32, 21.9) * mm, v(24.26, 22.2) * mm, v(25.5, 22.17) * mm, v(26.3, 21.88) * mm, v(27.22, 21.27) * mm, v(27.8, 20.58) * mm, v(28.17, 19.83) * mm, v(28.33, 19.17) * mm, v(28.35, 18.54) * mm, v(28.22, 17.7) * mm, v(28.07, 17.31) * mm], "startDerivative": vector(5.68, 3.18) * mm, "endDerivative": vector(-2.48, -5.08) * mm});
            skFitSpline(sketch, "E16", {"points": [v(26.66, 17.43) * mm, v(26.85, 17.8) * mm, v(27, 18.43) * mm, v(26.95, 19.3) * mm, v(26.46, 20.14) * mm, v(25.65, 20.76) * mm, v(24.86, 20.97) * mm, v(24.13, 20.96) * mm, v(23.65, 20.76) * mm, v(23.53, 20.69) * mm], "startDerivative": vector(2.16, 3.92) * mm, "endDerivative": vector(-1.95, -1.24) * mm});
            skFitSpline(sketch, "E17", {"points": [v(19.08, 8.92) * mm, v(19.11, 10.05) * mm, v(18.68, 11.3) * mm, v(17.78, 12.36) * mm, v(17, 12.85) * mm, v(15.73, 13.15) * mm, v(14.82, 13.07) * mm, v(13.45, 12.47) * mm, v(12.3, 11.06) * mm, v(12, 9.92) * mm, v(12.06, 8.68) * mm, v(12.77, 7.23) * mm, v(13.44, 6.6) * mm, v(14.34, 6.12) * mm, v(15.4, 5.92) * mm, v(16.83, 6.12) * mm, v(18.02, 6.9) * mm, v(18.71, 7.8) * mm, v(19.08, 8.92) * mm]});
            skFitSpline(sketch, "E18", {"points": [v(14.24, 11.5) * mm, v(13.71, 11.01) * mm, v(13.31, 10.25) * mm, v(13.2, 9.42) * mm, v(13.54, 8.38) * mm, v(14.26, 7.6) * mm, v(15.38, 7.24) * mm, v(16.38, 7.43) * mm, v(17.3, 8.18) * mm, v(17.68, 8.96) * mm, v(17.76, 9.87) * mm, v(17.5, 10.66) * mm, v(16.95, 11.3) * mm, v(16.34, 11.68) * mm, v(15.43, 11.83) * mm, v(14.83, 11.74) * mm, v(14.24, 11.5) * mm]});
            skFitSpline(sketch, "E19", {"points": [v(-9.53, -12.91) * mm, v(-9.53, -11.97) * mm, v(-9.37, -10.73) * mm, v(-8.99, -9.13) * mm, v(-8.63, -7.78) * mm, v(-8.58, -6.39) * mm, v(-8.65, -6.9) * mm, v(-8.76, -7.77) * mm, v(-9.32, -8.96) * mm, v(-10.46, -9.64) * mm, v(-12.7, -11.02) * mm, v(-14.65, -12.58) * mm, v(-16.3, -13.81) * mm, v(-19.17, -15.43) * mm, v(-22.08, -16.2) * mm, v(-23.98, -16.49) * mm, v(-26.57, -16.66) * mm, v(-28.55, -16.57) * mm, v(-31.02, -16.34) * mm], "startDerivative": vector(-0.63, 22.67) * mm, "endDerivative": vector(-38.96, 4.18) * mm});
            skFitSpline(sketch, "E20", {"points": [v(12.27, -8.08) * mm, v(12.27, -7.41) * mm, v(12.11, -6.53) * mm, v(11.75, -6.1) * mm, v(11.2, -5.45) * mm, v(11.1, -4.78) * mm, v(11.26, -5.28) * mm, v(11.94, -5.83) * mm, v(13.4, -5.42) * mm, v(15.03, -4.75) * mm, v(16.43, -4.18) * mm], "startDerivative": vector(0.22, 7.43) * mm, "endDerivative": vector(10.87, 4.5) * mm});
            skFitSpline(sketch, "E21", {"points": [v(6.96, 3.44) * mm, v(7.18, 3.87) * mm, v(7.63, 4.21) * mm, v(8.98, 3.76) * mm, v(9.54, 3.22) * mm, v(10.18, 2.66) * mm], "startDerivative": vector(1.3, 2.73) * mm, "endDerivative": vector(3.36, -2.67) * mm});
            skFitSpline(sketch, "E22", {"points": [v(25.13, 13.97) * mm, v(24.98, 13.9) * mm, v(24.9, 13.71) * mm, v(24.96, 13.56) * mm, v(25.26, 13.44) * mm, v(25.6, 13.51) * mm, v(25.7, 13.66) * mm, v(25.56, 13.84) * mm, v(25.33, 13.94) * mm, v(25.13, 13.97) * mm]});
            skFitSpline(sketch, "E23", {"points": [v(27.51, 16.6) * mm, v(27.55, 16.53) * mm, v(27.78, 16.38) * mm, v(27.92, 16.28) * mm, v(28.01, 16.23) * mm, v(28.12, 16.19) * mm, v(28.15, 16.23) * mm, v(28.06, 16.34) * mm, v(27.88, 16.44) * mm, v(27.71, 16.51) * mm, v(27.62, 16.6) * mm, v(27.56, 16.62) * mm, v(27.51, 16.6) * mm]});
            skFitSpline(sketch, "E24", {"points": [v(30.7, 17.5) * mm, v(30.64, 17.4) * mm, v(30.28, 17.26) * mm, v(29.34, 17.04) * mm, v(28.28, 16.93) * mm, v(27.44, 16.95) * mm, v(26.78, 17.1) * mm, v(26.55, 17.23) * mm, v(26.48, 17.36) * mm, v(26.36, 17.41) * mm, v(26.27, 17.47) * mm, v(26.2, 17.57) * mm], "startDerivative": vector(-0.66, -2.04) * mm, "endDerivative": vector(-1.1, 2.22) * mm});
            skFitSpline(sketch, "E25", {"points": [v(17.84, 2.57) * mm, v(16.75, 1.79) * mm, v(16.33, 0.88) * mm, v(16.57, -0.08) * mm, v(17.18, -0.75) * mm, v(17.94, -1.38) * mm], "startDerivative": vector(-5.34, -3.12) * mm, "endDerivative": vector(4.03, -3.16) * mm});
            skFitSpline(sketch, "E26", {"points": [v(20.52, 4.14) * mm, v(22.64, 3.84) * mm, v(24.8, 3.97) * mm, v(26.39, 4.38) * mm, v(27.52, 4.47) * mm, v(29.48, 4.34) * mm, v(30.97, 3.82) * mm, v(31.72, 3.42) * mm, v(32.1, 3.21) * mm], "startDerivative": vector(13.64, -2.55) * mm, "endDerivative": vector(5.02, -2.91) * mm});
            skFitSpline(sketch, "E27", {"points": [v(25.26, -1.64) * mm, v(23.5, -1.46) * mm, v(21.74, -0.72) * mm, v(20.9, -0.06) * mm, v(20.41, 0.69) * mm, v(20.2, 0.87) * mm, v(20.34, 0.5) * mm, v(20.76, -0.17) * mm, v(21.66, -0.82) * mm, v(23.48, -1.6) * mm, v(24.84, -1.73) * mm], "startDerivative": vector(-15.8, 0.68) * mm, "endDerivative": vector(10.16, -0.54) * mm});
            skFitSpline(sketch, "E28", {"points": [v(29.17, 11.5) * mm, v(30.53, 10.16) * mm, v(31.38, 9.4) * mm, v(32.17, 8.35) * mm, v(32.71, 7.07) * mm, v(32.8, 5.98) * mm, v(32.67, 4.84) * mm, v(32.38, 3.78) * mm, v(32.1, 3.21) * mm, v(31.51, 2.46) * mm, v(29.61, 0.75) * mm, v(28.01, -0.2) * mm, v(26.28, -1.15) * mm, v(25.26, -1.64) * mm], "startDerivative": vector(15.37, -15.74) * mm, "endDerivative": vector(-13.14, -5.98) * mm});
            skFitSpline(sketch, "E29", {"points": [v(19.31, 3.37) * mm, v(20.53, 3.52) * mm, v(22.4, 3.23) * mm, v(23.84, 2.58) * mm, v(25.48, 1.52) * mm, v(26.41, 0.91) * mm, v(27.83, 0.45) * mm, v(28.9, 0.28) * mm], "startDerivative": vector(8.66, 1.68) * mm, "endDerivative": vector(8.23, -1) * mm});
            skFitSpline(sketch, "E30", {"points": [v(10.83, 14.46) * mm, v(12.16, 15.45) * mm, v(14.19, 16.34) * mm, v(16.28, 16.54) * mm, v(18.08, 16.03) * mm, v(19.55, 14.99) * mm, v(20.7, 13.83) * mm, v(21.6, 12.08) * mm, v(21.98, 10.19) * mm, v(21.7, 8.4) * mm, v(20.85, 6.52) * mm, v(19.55, 4.94) * mm, v(17.83, 3.85) * mm, v(15.54, 3.28) * mm, v(12.83, 3.95) * mm, v(11.65, 5.03) * mm, v(10.7, 6.24) * mm, v(9.88, 7.72) * mm, v(9.36, 9.27) * mm, v(9.23, 11.12) * mm, v(9.51, 12.73) * mm, v(10.24, 13.89) * mm, v(10.83, 14.46) * mm]});
            skFitSpline(sketch, "E31", {"points": [v(24.07, 14.8) * mm, v(24.31, 14.8) * mm, v(24.53, 14.94) * mm, v(24.48, 15.28) * mm, v(24.2, 15.53) * mm, v(23.9, 15.52) * mm, v(23.82, 15.33) * mm, v(23.8, 15.07) * mm, v(23.9, 14.89) * mm, v(24.07, 14.8) * mm]});
            skFitSpline(sketch, "E32", {"points": [v(23.9, 15.52) * mm, v(23.76, 15.75) * mm, v(23.48, 15.97) * mm, v(23.15, 15.9) * mm, v(23.01, 15.68) * mm, v(23.02, 15.53) * mm, v(23.21, 15.28) * mm, v(23.54, 15.02) * mm, v(23.8, 15.07) * mm], "startDerivative": vector(-1.1, 1.84) * mm, "endDerivative": vector(2.16, 0.9) * mm});
            skFitSpline(sketch, "E33", {"points": [v(23.15, 15.9) * mm, v(23, 16.21) * mm, v(22.72, 16.43) * mm, v(22.31, 16.5) * mm, v(22.08, 16.36) * mm, v(21.96, 16.24) * mm, v(22.06, 16.02) * mm, v(22.27, 15.74) * mm, v(22.57, 15.53) * mm, v(22.83, 15.42) * mm, v(23.02, 15.53) * mm], "startDerivative": vector(-1.02, 3.15) * mm, "endDerivative": vector(2.15, 1.75) * mm});
            skFitSpline(sketch, "E34", {"points": [v(22.31, 16.5) * mm, v(22.18, 16.85) * mm, v(22.12, 16.94) * mm, v(21.65, 17.08) * mm, v(21.18, 17.25) * mm, v(20.9, 16.93) * mm, v(20.92, 16.73) * mm, v(21.06, 16.58) * mm, v(21.14, 16.37) * mm, v(21.5, 16.2) * mm, v(21.78, 16.13) * mm, v(21.96, 16.24) * mm], "startDerivative": vector(-1.63, 4.02) * mm, "endDerivative": vector(2.26, 1.94) * mm});
            skFitSpline(sketch, "E35", {"points": [v(21.18, 17.25) * mm, v(21.02, 17.45) * mm, v(20.75, 17.76) * mm, v(20.6, 17.94) * mm, v(20.02, 18.1) * mm, v(19.74, 18.2) * mm, v(19.64, 17.87) * mm, v(19.7, 17.6) * mm, v(19.88, 17.32) * mm, v(20.29, 17.06) * mm, v(20.46, 16.88) * mm, v(20.72, 16.86) * mm, v(20.9, 16.93) * mm], "startDerivative": vector(-1.91, 2.46) * mm, "endDerivative": vector(2.57, 1.35) * mm});
            skFitSpline(sketch, "E36", {"points": [v(19.74, 18.2) * mm, v(19.37, 18.5) * mm, v(19.03, 18.79) * mm, v(18.42, 18.9) * mm, v(18.23, 18.89) * mm, v(18, 18.45) * mm, v(18, 18.2) * mm, v(18.36, 17.79) * mm, v(18.86, 17.64) * mm, v(19.26, 17.64) * mm, v(19.53, 17.66) * mm, v(19.66, 17.74) * mm], "startDerivative": vector(-3.83, 2.9) * mm, "endDerivative": vector(2, 1.55) * mm});
            skFitSpline(sketch, "E37", {"points": [v(18.23, 18.89) * mm, v(18.13, 19.07) * mm, v(17.67, 19.4) * mm, v(17.2, 19.66) * mm, v(16.36, 19.71) * mm, v(15.96, 19.7) * mm, v(15.8, 19.47) * mm, v(15.88, 19.2) * mm, v(15.93, 19) * mm, v(16.5, 18.74) * mm, v(17.19, 18.48) * mm, v(17.65, 18.32) * mm, v(17.87, 18.28) * mm, v(18, 18.45) * mm], "startDerivative": vector(-1.07, 3.23) * mm, "endDerivative": vector(1.8, 3.93) * mm});
            skFitSpline(sketch, "E38", {"points": [v(15.96, 19.7) * mm, v(15.44, 19.95) * mm, v(15, 20.15) * mm, v(14.28, 20.17) * mm, v(13.7, 20) * mm, v(13.46, 19.86) * mm, v(13.38, 19.47) * mm, v(13.65, 18.98) * mm, v(14.38, 18.8) * mm, v(15.28, 18.98) * mm, v(15.75, 19.18) * mm, v(15.88, 19.2) * mm], "startDerivative": vector(-5.61, 2.58) * mm, "endDerivative": vector(2.57, 0.14) * mm});
            skFitSpline(sketch, "E39", {"points": [v(13.46, 19.86) * mm, v(13.14, 20.07) * mm, v(12.45, 20.16) * mm, v(11.56, 19.86) * mm, v(10.96, 19.6) * mm, v(11.2, 18.8) * mm, v(11.65, 18.82) * mm, v(11.9, 18.75) * mm, v(12.47, 18.6) * mm, v(12.86, 18.76) * mm, v(13.16, 19.02) * mm, v(13.33, 19.28) * mm, v(13.38, 19.47) * mm], "startDerivative": vector(-3.7, 3.15) * mm, "endDerivative": vector(0.26, 4) * mm});
            skFitSpline(sketch, "E40", {"points": [v(10.96, 19.6) * mm, v(9.81, 19.56) * mm, v(8.82, 19.06) * mm, v(8.2, 18.67) * mm, v(8.29, 18.16) * mm, v(8.6, 17.7) * mm, v(9.17, 17.77) * mm, v(9.73, 17.76) * mm, v(10.5, 18.07) * mm, v(11.07, 18.35) * mm, v(11.21, 18.6) * mm, v(11.2, 18.8) * mm], "startDerivative": vector(-9.58, 0.68) * mm, "endDerivative": vector(-0.59, 3.93) * mm});
            skFitSpline(sketch, "E41", {"points": [v(8.18, 18.45) * mm, v(7.48, 18.23) * mm, v(6.73, 17.83) * mm, v(6.23, 17.21) * mm, v(6, 16.68) * mm, v(6.04, 16.44) * mm, v(6.24, 16.17) * mm, v(6.63, 16.29) * mm, v(7.26, 16.54) * mm, v(7.4, 16.84) * mm, v(7.86, 17.2) * mm, v(8.18, 17.58) * mm, v(8.29, 18.16) * mm], "startDerivative": vector(-7.06, -2.1) * mm, "endDerivative": vector(-0.45, 6.8) * mm});
            skFitSpline(sketch, "E42", {"points": [v(6.23, 17.21) * mm, v(5.77, 16.93) * mm, v(5.33, 16.55) * mm, v(5.12, 16.14) * mm, v(5.04, 15.79) * mm, v(5.05, 15.47) * mm, v(5.24, 15.44) * mm, v(5.6, 15.4) * mm, v(5.81, 15.53) * mm, v(6.14, 16) * mm, v(6.24, 16.17) * mm], "startDerivative": vector(-3.78, -2.2) * mm, "endDerivative": vector(1.75, 1.46) * mm});
            skFitSpline(sketch, "E43", {"points": [v(5.04, 15.79) * mm, v(4.7, 15.52) * mm, v(4.36, 15.06) * mm, v(4.27, 14.6) * mm, v(4.26, 14.17) * mm, v(4.4, 13.8) * mm, v(4.57, 13.54) * mm, v(4.63, 13.92) * mm, v(4.68, 14.35) * mm, v(4.84, 15.03) * mm, v(4.98, 15.41) * mm, v(5.05, 15.47) * mm], "startDerivative": vector(-3.54, -2.56) * mm, "endDerivative": vector(1.57, 0.96) * mm});
            skFitSpline(sketch, "E44", {"points": [v(4.26, 14.43) * mm, v(4, 14.34) * mm, v(3.85, 13.8) * mm, v(3.93, 13.3) * mm, v(4.06, 13) * mm, v(4.12, 13.1) * mm, v(4.26, 13.52) * mm, v(4.4, 13.8) * mm], "startDerivative": vector(-2.17, -0.2) * mm, "endDerivative": vector(1.04, 1.81) * mm});
            skLineSegment(sketch, "E45", {"start": v(3.85, 13.8) * mm, "end": v(3.7, 13.73) * mm});
            skFitSpline(sketch, "E46", {"points": [v(26.55, 17.23) * mm, v(26.55, 17.02) * mm, v(26.41, 16.92) * mm, v(26.13, 17) * mm, v(26.04, 17.23) * mm, v(26.06, 17.34) * mm, v(26.27, 17.47) * mm], "startDerivative": vector(0.2, -1.33) * mm, "endDerivative": vector(1.44, 0.63) * mm});
            skFitSpline(sketch, "E47", {"points": [v(25.78, 17.94) * mm, v(25.54, 17.93) * mm, v(25.4, 17.8) * mm, v(25.37, 17.6) * mm, v(25.6, 17.4) * mm, v(25.84, 17.4) * mm, v(25.98, 17.52) * mm, v(26, 17.72) * mm], "startDerivative": vector(-1.76, 0.12) * mm, "endDerivative": vector(-0.02, 1.62) * mm});
            skFitSpline(sketch, "E48", {"points": [v(25.16, 18.66) * mm, v(25.03, 18.68) * mm, v(24.76, 18.63) * mm, v(24.6, 18.45) * mm, v(24.7, 18.17) * mm, v(24.89, 17.96) * mm, v(25.1, 17.91) * mm, v(25.3, 17.96) * mm, v(25.43, 18.07) * mm, v(25.5, 18.33) * mm], "startDerivative": vector(-1.41, 0.29) * mm, "endDerivative": vector(-0.64, 3.07) * mm});
            skFitSpline(sketch, "E49", {"points": [v(24.93, 19.06) * mm, v(24.89, 18.92) * mm, v(24.66, 18.78) * mm, v(24.27, 18.82) * mm, v(24.04, 18.98) * mm, v(23.98, 19.3) * mm, v(24.06, 19.5) * mm, v(24.28, 19.55) * mm, v(24.44, 19.57) * mm], "startDerivative": vector(-0.12, -1.47) * mm, "endDerivative": vector(1.45, 0.24) * mm});
            skFitSpline(sketch, "E50", {"points": [v(24.21, 19.89) * mm, v(24.17, 19.73) * mm, v(23.93, 19.61) * mm, v(23.58, 19.61) * mm, v(23.34, 19.76) * mm, v(23.1, 20.07) * mm, v(23.06, 20.38) * mm, v(23.2, 20.53) * mm, v(23.54, 20.64) * mm], "startDerivative": vector(-0.17, -1.78) * mm, "endDerivative": vector(2.54, 0.66) * mm});
            skFitSpline(sketch, "E51", {"points": [v(23.27, 21.02) * mm, v(23.3, 20.86) * mm, v(23.15, 20.76) * mm, v(22.7, 20.77) * mm, v(22.29, 21.02) * mm, v(22.1, 21.25) * mm, v(22.13, 21.64) * mm, v(22.39, 21.85) * mm, v(22.6, 21.83) * mm, v(22.8, 21.7) * mm, v(22.92, 21.6) * mm], "startDerivative": vector(1.01, -2.25) * mm, "endDerivative": vector(1.6, -1.36) * mm});
            skFitSpline(sketch, "E52", {"points": [v(21.9, 23.14) * mm, v(21.17, 23.35) * mm, v(20.68, 22.97) * mm, v(20.65, 22.48) * mm, v(20.8, 22.05) * mm, v(21.18, 21.78) * mm, v(21.78, 21.6) * mm, v(22.2, 21.81) * mm, v(22.47, 21.97) * mm, v(22.46, 22.21) * mm, v(22.25, 22.77) * mm, v(21.9, 23.14) * mm]});
            skFitSpline(sketch, "E53", {"points": [v(20.44, 22.98) * mm, v(20.9, 23.45) * mm, v(21.2, 24.17) * mm, v(20.96, 24.56) * mm, v(20.5, 24.9) * mm, v(20.1, 24.93) * mm, v(19.84, 24.67) * mm, v(19.65, 24.18) * mm, v(19.74, 23.67) * mm, v(19.99, 23.13) * mm, v(20.26, 22.93) * mm, v(20.44, 22.98) * mm]});
            skFitSpline(sketch, "E54", {"points": [v(19.39, 24.7) * mm, v(20.03, 25.02) * mm, v(20.41, 25.5) * mm, v(19.92, 26.13) * mm, v(19.4, 26.3) * mm, v(18.88, 26.12) * mm, v(18.62, 25.68) * mm, v(18.75, 25.1) * mm, v(18.98, 24.84) * mm, v(19.39, 24.7) * mm]});
            skFitSpline(sketch, "E55", {"points": [v(18.21, 27.39) * mm, v(17.9, 27.08) * mm, v(17.56, 26.54) * mm, v(17.6, 26.17) * mm, v(17.76, 26.18) * mm, v(18.64, 26.54) * mm, v(19.34, 26.87) * mm, v(19.59, 27.09) * mm], "startDerivative": vector(-2.26, -2.03) * mm, "endDerivative": vector(1.8, 1.94) * mm});
            skFitSpline(sketch, "E56", {"points": [v(17.08, 26.9) * mm, v(16.74, 26.2) * mm, v(16.75, 26.1) * mm, v(17.15, 26.18) * mm, v(17.54, 26.44) * mm], "startDerivative": vector(-1.26, -2.33) * mm, "endDerivative": vector(1.3, 1) * mm});
            skFitSpline(sketch, "E57", {"points": [v(16.03, 25.76) * mm, v(16.09, 25.68) * mm, v(16.4, 25.82) * mm, v(16.62, 26) * mm, v(16.73, 26.14) * mm, v(16.73, 26.14) * mm], "startDerivative": vector(0.23, -0.62) * mm, "endDerivative": vector(-0.02, -0.1) * mm});
            skFitSpline(sketch, "E58", {"points": [v(15.61, 25.1) * mm, v(15.65, 25.05) * mm, v(15.94, 25.2) * mm, v(16.03, 25.46) * mm, v(16.09, 25.68) * mm], "startDerivative": vector(0.14, -0.55) * mm, "endDerivative": vector(0.25, 0.84) * mm});
            skFitSpline(sketch, "E59", {"points": [v(13.92, 21.3) * mm, v(13.7, 21.18) * mm, v(13.48, 21.16) * mm, v(13.3, 21.4) * mm, v(13.4, 21.6) * mm, v(13.65, 21.74) * mm, v(13.72, 21.73) * mm, v(13.82, 21.56) * mm, v(13.92, 21.3) * mm]});
            skFitSpline(sketch, "E60", {"points": [v(12.83, 21.8) * mm, v(13.1, 21.84) * mm, v(13.16, 21.93) * mm, v(13.12, 22.15) * mm, v(12.95, 22.3) * mm, v(12.8, 22.3) * mm, v(12.57, 22.14) * mm, v(12.56, 22) * mm, v(12.6, 21.88) * mm, v(12.83, 21.8) * mm]});
            skFitSpline(sketch, "E61", {"points": [v(12.32, 22.22) * mm, v(12.22, 22.02) * mm, v(11.96, 21.9) * mm, v(11.71, 21.98) * mm, v(11.75, 22.27) * mm, v(11.92, 22.48) * mm, v(12.05, 22.48) * mm, v(12.2, 22.4) * mm, v(12.32, 22.22) * mm]});
            skFitSpline(sketch, "E62", {"points": [v(11.55, 22.93) * mm, v(11.45, 22.83) * mm, v(11.37, 22.7) * mm, v(11.47, 22.52) * mm, v(11.6, 22.48) * mm, v(11.8, 22.55) * mm, v(11.96, 22.68) * mm, v(11.98, 22.73) * mm], "startDerivative": vector(-0.64, -0.73) * mm, "endDerivative": vector(0.13, 0.55) * mm});
            skFitSpline(sketch, "E63", {"points": [v(10.82, 22.98) * mm, v(10.68, 22.93) * mm, v(10.56, 22.81) * mm, v(10.62, 22.61) * mm, v(10.77, 22.53) * mm, v(11, 22.6) * mm, v(11.1, 22.77) * mm, v(11.06, 22.88) * mm, v(10.93, 22.97) * mm, v(10.82, 22.98) * mm]});
            skFitSpline(sketch, "E64", {"points": [v(10.61, 23.3) * mm, v(10.61, 23.2) * mm, v(10.48, 23.1) * mm, v(10.2, 23.04) * mm, v(10.03, 23.12) * mm, v(10, 23.3) * mm, v(10.06, 23.43) * mm], "startDerivative": vector(0.16, -0.78) * mm, "endDerivative": vector(0.47, 0.83) * mm});
            skFitSpline(sketch, "E65", {"points": [v(9.42, 23.3) * mm, v(9.22, 23.05) * mm, v(9.28, 22.75) * mm, v(9.45, 22.62) * mm, v(9.72, 22.65) * mm, v(9.81, 22.86) * mm, v(9.71, 23.23) * mm, v(9.42, 23.3) * mm]});
            skFitSpline(sketch, "E66", {"points": [v(9.03, 23.2) * mm, v(8.81, 22.86) * mm, v(8.66, 22.85) * mm, v(8.45, 22.95) * mm, v(8.47, 23.3) * mm, v(8.68, 23.5) * mm, v(8.86, 23.5) * mm, v(9.03, 23.2) * mm]});
            skFitSpline(sketch, "E67", {"points": [v(8.37, 23.77) * mm, v(8.23, 23.6) * mm, v(8.27, 23.43) * mm, v(8.47, 23.3) * mm], "startDerivative": vector(-0.52, -0.48) * mm, "endDerivative": vector(0.66, -0.33) * mm});
            skFitSpline(sketch, "E68", {"points": [v(8.86, 23.7) * mm, v(8.9, 23.59) * mm, v(8.86, 23.5) * mm], "startDerivative": vector(0.14, -0.23) * mm, "endDerivative": vector(-0.15, -0.17) * mm});
            skFitSpline(sketch, "E69", {"points": [v(7.43, 23.81) * mm, v(7.26, 23.61) * mm, v(7.14, 23.38) * mm, v(7.38, 23.22) * mm, v(7.89, 23.36) * mm, v(8.08, 23.48) * mm, v(8, 23.64) * mm, v(7.85, 23.77) * mm], "startDerivative": vector(-1.1, -1.35) * mm, "endDerivative": vector(-1.17, 0.91) * mm});
            skFitSpline(sketch, "E70", {"points": [v(6.62, 23.65) * mm, v(6.35, 23.4) * mm, v(6.38, 23.24) * mm, v(6.63, 23.25) * mm, v(6.81, 23.39) * mm, v(6.8, 23.56) * mm, v(6.62, 23.65) * mm]});
            skFitSpline(sketch, "E71", {"points": [v(4.9, 23.23) * mm, v(4.86, 23.03) * mm, v(4.81, 22.86) * mm, v(4.66, 22.9) * mm, v(4.52, 22.77) * mm, v(4.4, 22.75) * mm, v(4.3, 22.7) * mm, v(4.13, 22.83) * mm], "startDerivative": vector(-0.3, -1.2) * mm, "endDerivative": vector(-1.12, 1.06) * mm});
            skFitSpline(sketch, "E72", {"points": [v(3.54, 22.32) * mm, v(3.76, 22.35) * mm, v(3.97, 22.39) * mm, v(4.03, 22.64) * mm, v(4.1, 22.82) * mm], "startDerivative": vector(1.06, -0.46) * mm, "endDerivative": vector(-0.29, 0.86) * mm});
            skFitSpline(sketch, "E73", {"points": [v(-23.47, -11.81) * mm, v(-22.76, -11.68) * mm, v(-22.24, -11.58) * mm, v(-21.21, -11.24) * mm, v(-19.95, -10.85) * mm, v(-19.03, -10.24) * mm, v(-17.71, -9.05) * mm, v(-17.12, -8.34) * mm, v(-16.45, -7.25) * mm, v(-16, -6.2) * mm, v(-15.88, -5.93) * mm, v(-15.7, -5.73) * mm, v(-15.5, -5.47) * mm, v(-15.41, -5.2) * mm, v(-15.25, -4.93) * mm, v(-15.06, -4.72) * mm, v(-14.99, -4.46) * mm, v(-14.89, -4.13) * mm, v(-14.6, -3.55) * mm, v(-14.22, -2.98) * mm, v(-14.2, -2.83) * mm, v(-13.87, -2.07) * mm, v(-13.43, -1.27) * mm, v(-13.14, -0.71) * mm, v(-12.9, 0.12) * mm, v(-12.43, 1.03) * mm, v(-12.25, 1.72) * mm, v(-12.04, 2.1) * mm, v(-11.99, 2.24) * mm, v(-11.93, 2.37) * mm, v(-11.93, 2.61) * mm, v(-11.76, 2.8) * mm, v(-11.59, 3.01) * mm, v(-11.46, 3.2) * mm, v(-11.43, 3.38) * mm, v(-11.41, 3.58) * mm, v(-11.4, 3.8) * mm, v(-11.33, 4) * mm, v(-11.25, 4.26) * mm, v(-11.08, 4.68) * mm, v(-10.85, 5.2) * mm, v(-10.72, 5.39) * mm, v(-10.6, 5.85) * mm, v(-10.43, 6.6) * mm, v(-10.2, 7.03) * mm, v(-9.86, 7.63) * mm, v(-9.53, 8.43) * mm, v(-9.22, 9.05) * mm, v(-8.85, 9.76) * mm, v(-8.23, 10.6) * mm, v(-7.43, 11.5) * mm, v(-6.71, 12.27) * mm, v(-6.27, 13) * mm, v(-5.26, 14.02) * mm, v(-3.8, 15.11) * mm, v(-2.04, 15.87) * mm, v(-1.08, 16.37) * mm, v(0.62, 16.53) * mm, v(1.98, 16.58) * mm, v(3.15, 16.63) * mm, v(3.51, 16.7) * mm], "startDerivative": vector(55.51, 11.33) * mm, "endDerivative": vector(23.68, 7.43) * mm});
            skSolve(sketch);
        }
        {
            var Q0;
            {var subQ0=sQuery(id+"F0.wireOp",EDGE,"E44");var subQ4=makeQuery(id+"F0.imprint","IMPRINT",VERTEX,{"derivedFrom":subQ0});Q0=makeQuery(id+"F0.imprint","IMPRINT",FACE,{"disambiguationData":[TD([[makeQuery(id+"F0.imprint","IMPRINT",EDGE,{"disambiguationData":[TD([[subQ4,1.0]])],"derivedFrom":subQ0}),1.0]])]});}
            var Q1;
            {var subQ0=sQuery(id+"F0.wireOp",EDGE,"E43");var subQ1=sQuery(id+"F0.wireOp",EDGE,"E42");var subQ2=makeQuery(id+"F0.imprint","INTERSECT",VERTEX,{"disambiguationData":[OD(0.0)],"derivedFrom":[subQ1,subQ0]});Q1=makeQuery(id+"F0.imprint","IMPRINT",FACE,{"disambiguationData":[TD([[makeQuery(id+"F0.imprint","IMPRINT",EDGE,{"disambiguationData":[TD([[subQ2,-1.0]])],"derivedFrom":subQ1}),-1.0]])]});}
            var Q2;
            {var subQ0=sQuery(id+"F0.wireOp",EDGE,"E42");var subQ1=sQuery(id+"F0.wireOp",EDGE,"E41");var subQ2=makeQuery(id+"F0.imprint","INTERSECT",VERTEX,{"disambiguationData":[OD(0.0)],"derivedFrom":[subQ1,subQ0]});Q2=makeQuery(id+"F0.imprint","IMPRINT",FACE,{"disambiguationData":[TD([[makeQuery(id+"F0.imprint","IMPRINT",EDGE,{"disambiguationData":[TD([[subQ2,-1.0]])],"derivedFrom":subQ1}),-1.0]])]});}
            var Q3;
            {var subQ0=sQuery(id+"F0.wireOp",EDGE,"E41");var subQ1=sQuery(id+"F0.wireOp",EDGE,"E40");var subQ2=makeQuery(id+"F0.imprint","INTERSECT",VERTEX,{"disambiguationData":[OD(0.0)],"derivedFrom":[subQ1,subQ0]});Q3=makeQuery(id+"F0.imprint","IMPRINT",FACE,{"disambiguationData":[TD([[makeQuery(id+"F0.imprint","IMPRINT",EDGE,{"disambiguationData":[TD([[subQ2,-1.0]])],"derivedFrom":subQ1}),-1.0]])]});}
            var Q4;
            {var subQ0=sQuery(id+"F0.wireOp",EDGE,"E40");var subQ1=sQuery(id+"F0.wireOp",EDGE,"E39");var subQ2=makeQuery(id+"F0.imprint","INTERSECT",VERTEX,{"disambiguationData":[OD(0.0)],"derivedFrom":[subQ1,subQ0]});Q4=makeQuery(id+"F0.imprint","IMPRINT",FACE,{"disambiguationData":[TD([[makeQuery(id+"F0.imprint","IMPRINT",EDGE,{"disambiguationData":[TD([[subQ2,-1.0]])],"derivedFrom":subQ1}),-1.0]])]});}
            var Q5;
            {var subQ0=sQuery(id+"F0.wireOp",EDGE,"E39");var subQ1=sQuery(id+"F0.wireOp",EDGE,"E38");var subQ2=makeQuery(id+"F0.imprint","INTERSECT",VERTEX,{"disambiguationData":[OD(0.0)],"derivedFrom":[subQ1,subQ0]});Q5=makeQuery(id+"F0.imprint","IMPRINT",FACE,{"disambiguationData":[TD([[makeQuery(id+"F0.imprint","IMPRINT",EDGE,{"disambiguationData":[TD([[subQ2,-1.0]])],"derivedFrom":subQ1}),-1.0]])]});}
            var Q6;
            {var subQ0=sQuery(id+"F0.wireOp",EDGE,"E38");var subQ1=sQuery(id+"F0.wireOp",EDGE,"E37");var subQ2=makeQuery(id+"F0.imprint","INTERSECT",VERTEX,{"disambiguationData":[OD(0.0)],"derivedFrom":[subQ1,subQ0]});Q6=makeQuery(id+"F0.imprint","IMPRINT",FACE,{"disambiguationData":[TD([[makeQuery(id+"F0.imprint","IMPRINT",EDGE,{"disambiguationData":[TD([[subQ2,-1.0]])],"derivedFrom":subQ1}),-1.0]])]});}
            var Q7;
            {var subQ0=sQuery(id+"F0.wireOp",EDGE,"E37");var subQ1=sQuery(id+"F0.wireOp",EDGE,"E36");var subQ2=makeQuery(id+"F0.imprint","INTERSECT",VERTEX,{"disambiguationData":[OD(0.0)],"derivedFrom":[subQ1,subQ0]});Q7=makeQuery(id+"F0.imprint","IMPRINT",FACE,{"disambiguationData":[TD([[makeQuery(id+"F0.imprint","IMPRINT",EDGE,{"disambiguationData":[TD([[subQ2,-1.0]])],"derivedFrom":subQ1}),-1.0]])]});}
            var Q8;
            {var subQ0=sQuery(id+"F0.wireOp",EDGE,"E36");var subQ1=sQuery(id+"F0.wireOp",EDGE,"E35");var subQ2=makeQuery(id+"F0.imprint","INTERSECT",VERTEX,{"disambiguationData":[OD(0.0)],"derivedFrom":[subQ1,subQ0]});Q8=makeQuery(id+"F0.imprint","IMPRINT",FACE,{"disambiguationData":[TD([[makeQuery(id+"F0.imprint","IMPRINT",EDGE,{"disambiguationData":[TD([[subQ2,-1.0]])],"derivedFrom":subQ1}),-1.0]])]});}
            var Q9;
            {var subQ0=sQuery(id+"F0.wireOp",EDGE,"E35");var subQ1=sQuery(id+"F0.wireOp",EDGE,"E34");var subQ2=makeQuery(id+"F0.imprint","INTERSECT",VERTEX,{"disambiguationData":[OD(0.0)],"derivedFrom":[subQ1,subQ0]});Q9=makeQuery(id+"F0.imprint","IMPRINT",FACE,{"disambiguationData":[TD([[makeQuery(id+"F0.imprint","IMPRINT",EDGE,{"disambiguationData":[TD([[subQ2,-1.0]])],"derivedFrom":subQ1}),-1.0]])]});}
            var Q10;
            {var subQ0=sQuery(id+"F0.wireOp",EDGE,"E34");var subQ1=sQuery(id+"F0.wireOp",EDGE,"E33");var subQ2=makeQuery(id+"F0.imprint","INTERSECT",VERTEX,{"disambiguationData":[OD(0.0)],"derivedFrom":[subQ1,subQ0]});Q10=makeQuery(id+"F0.imprint","IMPRINT",FACE,{"disambiguationData":[TD([[makeQuery(id+"F0.imprint","IMPRINT",EDGE,{"disambiguationData":[TD([[subQ2,-1.0]])],"derivedFrom":subQ1}),-1.0]])]});}
            var Q11;
            {var subQ0=sQuery(id+"F0.wireOp",EDGE,"E33");var subQ1=sQuery(id+"F0.wireOp",EDGE,"E32");var subQ2=makeQuery(id+"F0.imprint","INTERSECT",VERTEX,{"disambiguationData":[OD(0.0)],"derivedFrom":[subQ1,subQ0]});Q11=makeQuery(id+"F0.imprint","IMPRINT",FACE,{"disambiguationData":[TD([[makeQuery(id+"F0.imprint","IMPRINT",EDGE,{"disambiguationData":[TD([[subQ2,-1.0]])],"derivedFrom":subQ1}),-1.0]])]});}
            var Q12;
            {var subQ0=sQuery(id+"F0.wireOp",EDGE,"E32");var subQ1=sQuery(id+"F0.wireOp",EDGE,"E31");var subQ2=makeQuery(id+"F0.imprint","INTERSECT",VERTEX,{"disambiguationData":[OD(0.0)],"derivedFrom":[subQ1,subQ0]});Q12=makeQuery(id+"F0.imprint","IMPRINT",FACE,{"disambiguationData":[TD([[makeQuery(id+"F0.imprint","IMPRINT",EDGE,{"disambiguationData":[TD([[subQ2,-1.0]])],"derivedFrom":subQ1}),-1.0]])]});}
            var Q13;
            {var subQ0=sQuery(id+"F0.wireOp",EDGE,"E32");var subQ1=sQuery(id+"F0.wireOp",EDGE,"E31");var subQ2=makeQuery(id+"F0.imprint","INTERSECT",VERTEX,{"disambiguationData":[OD(0.0)],"derivedFrom":[subQ1,subQ0]});Q13=makeQuery(id+"F0.imprint","IMPRINT",FACE,{"disambiguationData":[TD([[makeQuery(id+"F0.imprint","IMPRINT",EDGE,{"disambiguationData":[TD([[subQ2,-1.0]])],"derivedFrom":subQ1}),1.0]])]});}
            var Q14;
            Q14=makeQuery(id+"F0.imprint","IMPRINT",FACE,{"disambiguationData":[TD([[makeQuery(id+"F0.imprint","IMPRINT",EDGE,{"derivedFrom":sQuery(id+"F0.wireOp",EDGE,"E59")}),-1.0]])]});
            var Q15;
            Q15=makeQuery(id+"F0.imprint","IMPRINT",FACE,{"disambiguationData":[TD([[makeQuery(id+"F0.imprint","IMPRINT",EDGE,{"derivedFrom":sQuery(id+"F0.wireOp",EDGE,"E60")}),1.0]])]});
            var Q16;
            Q16=makeQuery(id+"F0.imprint","IMPRINT",FACE,{"disambiguationData":[TD([[makeQuery(id+"F0.imprint","IMPRINT",EDGE,{"derivedFrom":sQuery(id+"F0.wireOp",EDGE,"E61")}),-1.0]])]});
            var Q17;
            {var subQ0=sQuery(id+"F0.wireOp",EDGE,"E62");Q17=makeQuery(id+"F0.imprint","IMPRINT",FACE,{"disambiguationData":[TD([[makeQuery(id+"F0.imprint","IMPRINT",EDGE,{"derivedFrom":subQ0}),1.0]])]});}
            var Q18;
            Q18=makeQuery(id+"F0.imprint","IMPRINT",FACE,{"disambiguationData":[TD([[makeQuery(id+"F0.imprint","IMPRINT",EDGE,{"derivedFrom":sQuery(id+"F0.wireOp",EDGE,"E63")}),1.0]])]});
            var Q19;
            {var subQ0=sQuery(id+"F0.wireOp",EDGE,"E64");Q19=makeQuery(id+"F0.imprint","IMPRINT",FACE,{"disambiguationData":[TD([[makeQuery(id+"F0.imprint","IMPRINT",EDGE,{"derivedFrom":subQ0}),-1.0]])]});}
            var Q20;
            Q20=makeQuery(id+"F0.imprint","IMPRINT",FACE,{"disambiguationData":[TD([[makeQuery(id+"F0.imprint","IMPRINT",EDGE,{"derivedFrom":sQuery(id+"F0.wireOp",EDGE,"E65")}),1.0]])]});
            var Q21;
            {var subQ0=sQuery(id+"F0.wireOp",EDGE,"E66");var subQ1=makeQuery(id+"F0.imprint","INTERSECT",VERTEX,{"derivedFrom":[subQ0,sQuery(id+"F0.wireOp",EDGE,"E67")]});Q21=makeQuery(id+"F0.imprint","IMPRINT",FACE,{"disambiguationData":[TD([[makeQuery(id+"F0.imprint","IMPRINT",EDGE,{"disambiguationData":[TD([[subQ1,-1.0]])],"derivedFrom":subQ0}),-1.0]])]});}
            var Q22;
            {var subQ0=sQuery(id+"F0.wireOp",EDGE,"E67");Q22=makeQuery(id+"F0.imprint","IMPRINT",FACE,{"disambiguationData":[TD([[makeQuery(id+"F0.imprint","IMPRINT",EDGE,{"derivedFrom":subQ0}),1.0]])]});}
            var Q23;
            {var subQ0=sQuery(id+"F0.wireOp",EDGE,"E69");Q23=makeQuery(id+"F0.imprint","IMPRINT",FACE,{"disambiguationData":[TD([[makeQuery(id+"F0.imprint","IMPRINT",EDGE,{"derivedFrom":subQ0}),1.0]])]});}
            var Q24;
            Q24=makeQuery(id+"F0.imprint","IMPRINT",FACE,{"disambiguationData":[TD([[makeQuery(id+"F0.imprint","IMPRINT",EDGE,{"derivedFrom":sQuery(id+"F0.wireOp",EDGE,"E70")}),1.0]])]});
            var Q25;
            {var subQ0=sQuery(id+"F0.wireOp",EDGE,"E71");Q25=makeQuery(id+"F0.imprint","IMPRINT",FACE,{"disambiguationData":[TD([[makeQuery(id+"F0.imprint","IMPRINT",EDGE,{"derivedFrom":subQ0}),-1.0]])]});}
            var Q26;
            {var subQ0=sQuery(id+"F0.wireOp",EDGE,"E72");Q26=makeQuery(id+"F0.imprint","IMPRINT",FACE,{"disambiguationData":[TD([[makeQuery(id+"F0.imprint","IMPRINT",EDGE,{"derivedFrom":subQ0}),1.0]])]});}
            var Q27;
            {var subQ3=sQuery(id+"F0.wireOp",EDGE,"E58");Q27=makeQuery(id+"F0.imprint","IMPRINT",FACE,{"disambiguationData":[TD([[makeQuery(id+"F0.imprint","IMPRINT",EDGE,{"derivedFrom":subQ3}),1.0]])]});}
            var Q28;
            {var subQ0=sQuery(id+"F0.wireOp",EDGE,"E56");var subQ1=sQuery(id+"F0.wireOp",EDGE,"E0");var subQ2=makeQuery(id+"F0.imprint","INTERSECT",VERTEX,{"derivedFrom":[subQ1,subQ0]});Q28=makeQuery(id+"F0.imprint","IMPRINT",FACE,{"disambiguationData":[TD([[makeQuery(id+"F0.imprint","IMPRINT",EDGE,{"disambiguationData":[TD([[subQ2,1.0]])],"derivedFrom":subQ1}),-1.0]])]});}
            var Q29;
            {var subQ1=sQuery(id+"F0.wireOp",EDGE,"E55");var subQ5=sQuery(id+"F0.wireOp",EDGE,"E0");var subQ6=makeQuery(id+"F0.imprint","INTERSECT",VERTEX,{"disambiguationData":[OD(0.0)],"derivedFrom":[subQ5,subQ1]});Q29=makeQuery(id+"F0.imprint","IMPRINT",FACE,{"disambiguationData":[TD([[makeQuery(id+"F0.imprint","IMPRINT",EDGE,{"disambiguationData":[TD([[subQ6,1.0]])],"derivedFrom":subQ5}),-1.0]])]});}
            var Q30;
            {var subQ0=sQuery(id+"F0.wireOp",EDGE,"E55");var subQ1=sQuery(id+"F0.wireOp",EDGE,"E0");var subQ2=makeQuery(id+"F0.imprint","INTERSECT",VERTEX,{"disambiguationData":[OD(0.0)],"derivedFrom":[subQ1,subQ0]});Q30=makeQuery(id+"F0.imprint","IMPRINT",FACE,{"disambiguationData":[TD([[makeQuery(id+"F0.imprint","IMPRINT",EDGE,{"disambiguationData":[TD([[subQ2,-1.0]])],"derivedFrom":subQ1}),-1.0]])]});}
            var Q31;
            Q31=makeQuery(id+"F0.imprint","IMPRINT",FACE,{"disambiguationData":[TD([[makeQuery(id+"F0.imprint","IMPRINT",EDGE,{"derivedFrom":sQuery(id+"F0.wireOp",EDGE,"E54")}),1.0]])]});
            var Q32;
            Q32=makeQuery(id+"F0.imprint","IMPRINT",FACE,{"disambiguationData":[TD([[makeQuery(id+"F0.imprint","IMPRINT",EDGE,{"derivedFrom":sQuery(id+"F0.wireOp",EDGE,"E53")}),1.0]])]});
            var Q33;
            Q33=makeQuery(id+"F0.imprint","IMPRINT",FACE,{"disambiguationData":[TD([[makeQuery(id+"F0.imprint","IMPRINT",EDGE,{"derivedFrom":sQuery(id+"F0.wireOp",EDGE,"E52")}),1.0]])]});
            var Q34;
            {var subQ0=sQuery(id+"F0.wireOp",EDGE,"E51");Q34=makeQuery(id+"F0.imprint","IMPRINT",FACE,{"disambiguationData":[TD([[makeQuery(id+"F0.imprint","IMPRINT",EDGE,{"derivedFrom":subQ0}),-1.0]])]});}
            var Q35;
            {var subQ0=sQuery(id+"F0.wireOp",EDGE,"E50");Q35=makeQuery(id+"F0.imprint","IMPRINT",FACE,{"disambiguationData":[TD([[makeQuery(id+"F0.imprint","IMPRINT",EDGE,{"derivedFrom":subQ0}),-1.0]])]});}
            var Q36;
            {var subQ0=sQuery(id+"F0.wireOp",EDGE,"E49");Q36=makeQuery(id+"F0.imprint","IMPRINT",FACE,{"disambiguationData":[TD([[makeQuery(id+"F0.imprint","IMPRINT",EDGE,{"derivedFrom":subQ0}),-1.0]])]});}
            var Q37;
            {var subQ0=sQuery(id+"F0.wireOp",EDGE,"E48");Q37=makeQuery(id+"F0.imprint","IMPRINT",FACE,{"disambiguationData":[TD([[makeQuery(id+"F0.imprint","IMPRINT",EDGE,{"derivedFrom":subQ0}),1.0]])]});}
            var Q38;
            {var subQ0=sQuery(id+"F0.wireOp",EDGE,"E47");Q38=makeQuery(id+"F0.imprint","IMPRINT",FACE,{"disambiguationData":[TD([[makeQuery(id+"F0.imprint","IMPRINT",EDGE,{"derivedFrom":subQ0}),1.0]])]});}
            var Q39;
            {var subQ0=sQuery(id+"F0.wireOp",EDGE,"E46");Q39=makeQuery(id+"F0.imprint","IMPRINT",FACE,{"disambiguationData":[TD([[makeQuery(id+"F0.imprint","IMPRINT",EDGE,{"derivedFrom":subQ0}),-1.0]])]});}
            extrude(context, id + "F1", {"entities" : qUnion([Q0, Q1, Q2, Q3, Q4, Q5, Q6, Q7, Q8, Q9, Q10, Q11, Q12, Q13, Q14, Q15, Q16, Q17, Q18, Q19, Q20, Q21, Q22, Q23, Q24, Q25, Q26, Q27, Q28, Q29, Q30, Q31, Q32, Q33, Q34, Q35, Q36, Q37, Q38, Q39]), "depth" : 4.2 * mm, "offsetDistance" : 25 * mm});
        }
        {
            var Q0;
            {var subQ32=sQuery(id+"F0.wireOp",EDGE,"E21");Q0=makeQuery(id+"F0.imprint","IMPRINT",FACE,{"disambiguationData":[TD([[makeQuery(id+"F0.imprint","IMPRINT",EDGE,{"derivedFrom":subQ32}),1.0]])]});}
            var Q1;
            Q1=makeQuery(id+"F0.imprint","IMPRINT",FACE,{"disambiguationData":[TD([[makeQuery(id+"F0.imprint","IMPRINT",EDGE,{"derivedFrom":sQuery(id+"F0.wireOp",EDGE,"E18")}),1.0]])]});
            extrude(context, id + "F2", {"entities" : qUnion([Q0, Q1]), "operationType" : NewBodyOperationType.ADD, "depth" : 3.9 * mm, "offsetDistance" : 25 * mm});
        }
        {
            var Q0;
            {var subQ11=sQuery(id+"F0.wireOp",EDGE,"E3");Q0=makeQuery(id+"F0.imprint","IMPRINT",FACE,{"disambiguationData":[TD([[makeQuery(id+"F0.imprint","IMPRINT",EDGE,{"derivedFrom":subQ11}),-1.0]])]});}
            var Q1;
            Q1=makeQuery(id+"F0.imprint","IMPRINT",FACE,{"disambiguationData":[TD([[makeQuery(id+"F0.imprint","IMPRINT",EDGE,{"derivedFrom":sQuery(id+"F0.wireOp",EDGE,"E4")}),1.0]])]});
            var Q2;
            {var subQ0=sQuery(id+"F0.wireOp",EDGE,"E1");var subQ1=sQuery(id+"F0.wireOp",EDGE,"E0");var subQ2=makeQuery(id+"F0.imprint","INTERSECT",VERTEX,{"disambiguationData":[OD(1.0)],"derivedFrom":[subQ1,subQ0]});Q2=makeQuery(id+"F0.imprint","IMPRINT",FACE,{"disambiguationData":[TD([[makeQuery(id+"F0.imprint","IMPRINT",EDGE,{"disambiguationData":[TD([[subQ2,-1.0]])],"derivedFrom":subQ1}),-1.0]])]});}
            var Q3;
            Q3=makeQuery(id+"F0.imprint","IMPRINT",FACE,{"disambiguationData":[TD([[makeQuery(id+"F0.imprint","IMPRINT",EDGE,{"derivedFrom":sQuery(id+"F0.wireOp",EDGE,"E23")}),1.0]])]});
            var Q4;
            Q4=makeQuery(id+"F0.imprint","IMPRINT",FACE,{"disambiguationData":[TD([[makeQuery(id+"F0.imprint","IMPRINT",EDGE,{"derivedFrom":sQuery(id+"F0.wireOp",EDGE,"E22")}),1.0]])]});
            var Q5;
            Q5=makeQuery(id+"F0.imprint","IMPRINT",FACE,{"disambiguationData":[TD([[makeQuery(id+"F0.imprint","IMPRINT",EDGE,{"derivedFrom":sQuery(id+"F0.wireOp",EDGE,"E17")}),1.0]])]});
            extrude(context, id + "F3", {"entities" : qUnion([Q0, Q1, Q2, Q3, Q4, Q5]), "operationType" : NewBodyOperationType.ADD, "depth" : 3.6 * mm, "offsetDistance" : 25 * mm});
        }
        {
            var Q0;
            {var subQ0=sQuery(id+"F0.wireOp",EDGE,"E16");Q0=makeQuery(id+"F0.imprint","IMPRINT",FACE,{"disambiguationData":[TD([[makeQuery(id+"F0.imprint","IMPRINT",EDGE,{"derivedFrom":subQ0}),1.0]])]});}
            var Q1;
            {var subQ2=sQuery(id+"F0.wireOp",EDGE,"E25");Q1=makeQuery(id+"F0.imprint","IMPRINT",FACE,{"disambiguationData":[TD([[makeQuery(id+"F0.imprint","IMPRINT",EDGE,{"derivedFrom":subQ2}),-1.0]])]});}
            var Q2;
            {var subQ4=sQuery(id+"F0.wireOp",EDGE,"E3");Q2=makeQuery(id+"F0.imprint","IMPRINT",FACE,{"disambiguationData":[TD([[makeQuery(id+"F0.imprint","IMPRINT",EDGE,{"derivedFrom":subQ4}),1.0]])]});}
            var Q3;
            Q3=makeQuery(id+"F0.imprint","IMPRINT",FACE,{"disambiguationData":[TD([[makeQuery(id+"F0.imprint","IMPRINT",EDGE,{"derivedFrom":sQuery(id+"F0.wireOp",EDGE,"E4")}),-1.0]])]});
            extrude(context, id + "F4", {"entities" : qUnion([Q0, Q1, Q2, Q3]), "operationType" : NewBodyOperationType.ADD, "depth" : 3.3 * mm, "offsetDistance" : 25 * mm});
        }
        {
            var Q0;
            {var subQ0=sQuery(id+"F0.wireOp",EDGE,"E15");Q0=makeQuery(id+"F0.imprint","IMPRINT",FACE,{"disambiguationData":[TD([[makeQuery(id+"F0.imprint","IMPRINT",EDGE,{"derivedFrom":subQ0}),-1.0]])]});}
            var Q1;
            {var subQ18=sQuery(id+"F0.wireOp",EDGE,"E10");Q1=makeQuery(id+"F0.imprint","IMPRINT",FACE,{"disambiguationData":[TD([[makeQuery(id+"F0.imprint","IMPRINT",EDGE,{"derivedFrom":subQ18}),-1.0]])]});}
            var Q2;
            {var subQ0=sQuery(id+"F0.wireOp",EDGE,"E25");Q2=makeQuery(id+"F0.imprint","IMPRINT",FACE,{"disambiguationData":[TD([[makeQuery(id+"F0.imprint","IMPRINT",EDGE,{"derivedFrom":subQ0}),1.0]])]});}
            extrude(context, id + "F5", {"entities" : qUnion([Q0, Q1, Q2]), "operationType" : NewBodyOperationType.ADD, "depth" : 3 * mm, "offsetDistance" : 25 * mm});
        }
        {
            var Q0;
            {var subQ0=sQuery(id+"F0.wireOp",EDGE,"E26");Q0=makeQuery(id+"F0.imprint","IMPRINT",FACE,{"disambiguationData":[TD([[makeQuery(id+"F0.imprint","IMPRINT",EDGE,{"derivedFrom":subQ0}),-1.0]])]});}
            var Q1;
            {var subQ4=sQuery(id+"F0.wireOp",EDGE,"E15");Q1=makeQuery(id+"F0.imprint","IMPRINT",FACE,{"disambiguationData":[TD([[makeQuery(id+"F0.imprint","IMPRINT",EDGE,{"derivedFrom":subQ4}),1.0]])]});}
            var Q2;
            {var subQ0=sQuery(id+"F0.wireOp",EDGE,"E11");var subQ1=sQuery(id+"F0.wireOp",EDGE,"E0");var subQ2=makeQuery(id+"F0.imprint","INTERSECT",VERTEX,{"derivedFrom":[subQ1,subQ0]});Q2=makeQuery(id+"F0.imprint","IMPRINT",FACE,{"disambiguationData":[TD([[makeQuery(id+"F0.imprint","IMPRINT",EDGE,{"disambiguationData":[TD([[subQ2,1.0]])],"derivedFrom":subQ1}),1.0]])]});}
            var Q3;
            {var subQ0=sQuery(id+"F0.wireOp",EDGE,"E73");var subQ1=sQuery(id+"F0.wireOp",EDGE,"E11");var subQ2=makeQuery(id+"F0.imprint","INTERSECT",VERTEX,{"disambiguationData":[OD(2.0)],"derivedFrom":[subQ1,subQ0]});Q3=makeQuery(id+"F0.imprint","IMPRINT",FACE,{"disambiguationData":[TD([[makeQuery(id+"F0.imprint","IMPRINT",EDGE,{"disambiguationData":[TD([[subQ2,-1.0]])],"derivedFrom":subQ1}),1.0]])]});}
            var Q4;
            {var subQ0=sQuery(id+"F0.wireOp",EDGE,"E73");var subQ1=sQuery(id+"F0.wireOp",EDGE,"E11");var subQ2=makeQuery(id+"F0.imprint","INTERSECT",VERTEX,{"disambiguationData":[OD(4.0)],"derivedFrom":[subQ1,subQ0]});Q4=makeQuery(id+"F0.imprint","IMPRINT",FACE,{"disambiguationData":[TD([[makeQuery(id+"F0.imprint","IMPRINT",EDGE,{"disambiguationData":[TD([[subQ2,-1.0]])],"derivedFrom":subQ1}),1.0]])]});}
            var Q5;
            {var subQ0=sQuery(id+"F0.wireOp",EDGE,"E73");var subQ1=sQuery(id+"F0.wireOp",EDGE,"E11");var subQ2=makeQuery(id+"F0.imprint","INTERSECT",VERTEX,{"disambiguationData":[OD(6.0)],"derivedFrom":[subQ1,subQ0]});Q5=makeQuery(id+"F0.imprint","IMPRINT",FACE,{"disambiguationData":[TD([[makeQuery(id+"F0.imprint","IMPRINT",EDGE,{"disambiguationData":[TD([[subQ2,-1.0]])],"derivedFrom":subQ1}),1.0]])]});}
            var Q6;
            {var subQ0=sQuery(id+"F0.wireOp",EDGE,"E73");var subQ1=sQuery(id+"F0.wireOp",EDGE,"E11");var subQ2=makeQuery(id+"F0.imprint","INTERSECT",VERTEX,{"disambiguationData":[OD(8.0)],"derivedFrom":[subQ1,subQ0]});Q6=makeQuery(id+"F0.imprint","IMPRINT",FACE,{"disambiguationData":[TD([[makeQuery(id+"F0.imprint","IMPRINT",EDGE,{"disambiguationData":[TD([[subQ2,-1.0]])],"derivedFrom":subQ1}),1.0]])]});}
            var Q7;
            {var subQ0=sQuery(id+"F0.wireOp",EDGE,"E73");var subQ1=sQuery(id+"F0.wireOp",EDGE,"E11");var subQ2=makeQuery(id+"F0.imprint","INTERSECT",VERTEX,{"disambiguationData":[OD(0.0)],"derivedFrom":[subQ1,subQ0]});Q7=makeQuery(id+"F0.imprint","IMPRINT",FACE,{"disambiguationData":[TD([[makeQuery(id+"F0.imprint","IMPRINT",EDGE,{"disambiguationData":[TD([[subQ2,1.0]])],"derivedFrom":subQ1}),1.0]])]});}
            var Q8;
            {var subQ0=sQuery(id+"F0.wireOp",EDGE,"E13");Q8=makeQuery(id+"F0.imprint","IMPRINT",FACE,{"disambiguationData":[TD([[makeQuery(id+"F0.imprint","IMPRINT",EDGE,{"derivedFrom":subQ0}),1.0]])]});}
            var Q9;
            {var subQ0=sQuery(id+"F0.wireOp",EDGE,"E12");Q9=makeQuery(id+"F0.imprint","IMPRINT",FACE,{"disambiguationData":[TD([[makeQuery(id+"F0.imprint","IMPRINT",EDGE,{"derivedFrom":subQ0}),-1.0]])]});}
            var Q10;
            {var subQ3=sQuery(id+"F0.wireOp",EDGE,"E9");Q10=makeQuery(id+"F0.imprint","IMPRINT",FACE,{"disambiguationData":[TD([[makeQuery(id+"F0.imprint","IMPRINT",EDGE,{"derivedFrom":subQ3}),1.0]])]});}
            var Q11;
            {var subQ0=sQuery(id+"F0.wireOp",EDGE,"E5");Q11=makeQuery(id+"F0.imprint","IMPRINT",FACE,{"disambiguationData":[TD([[makeQuery(id+"F0.imprint","IMPRINT",EDGE,{"derivedFrom":subQ0}),-1.0]])]});}
            var Q12;
            {var subQ0=sQuery(id+"F0.wireOp",EDGE,"E27");Q12=makeQuery(id+"F0.imprint","IMPRINT",FACE,{"disambiguationData":[TD([[makeQuery(id+"F0.imprint","IMPRINT",EDGE,{"derivedFrom":subQ0}),1.0]])]});}
            extrude(context, id + "F6", {"entities" : qUnion([Q0, Q1, Q2, Q3, Q4, Q5, Q6, Q7, Q8, Q9, Q10, Q11, Q12]), "operationType" : NewBodyOperationType.ADD, "depth" : 2.7 * mm, "offsetDistance" : 25 * mm});
        }
        {
            var Q0;
            {var subQ0=sQuery(id+"F0.wireOp",EDGE,"E8");Q0=makeQuery(id+"F0.imprint","IMPRINT",FACE,{"disambiguationData":[TD([[makeQuery(id+"F0.imprint","IMPRINT",EDGE,{"derivedFrom":subQ0}),-1.0]])]});}
            var Q1;
            {var subQ0=sQuery(id+"F0.wireOp",EDGE,"E7");var subQ1=makeQuery(id+"F0.imprint","INTERSECT",VERTEX,{"derivedFrom":[subQ0,sQuery(id+"F0.wireOp",EDGE,"E10")]});Q1=makeQuery(id+"F0.imprint","IMPRINT",FACE,{"disambiguationData":[TD([[makeQuery(id+"F0.imprint","IMPRINT",EDGE,{"disambiguationData":[TD([[subQ1,1.0]])],"derivedFrom":subQ0}),1.0]])]});}
            var Q2;
            {var subQ0=sQuery(id+"F0.wireOp",EDGE,"E26");Q2=makeQuery(id+"F0.imprint","IMPRINT",FACE,{"disambiguationData":[TD([[makeQuery(id+"F0.imprint","IMPRINT",EDGE,{"derivedFrom":subQ0}),1.0]])]});}
            extrude(context, id + "F7", {"entities" : qUnion([Q0, Q1, Q2]), "operationType" : NewBodyOperationType.ADD, "depth" : 2.4 * mm, "offsetDistance" : 25 * mm});
        }
    });
